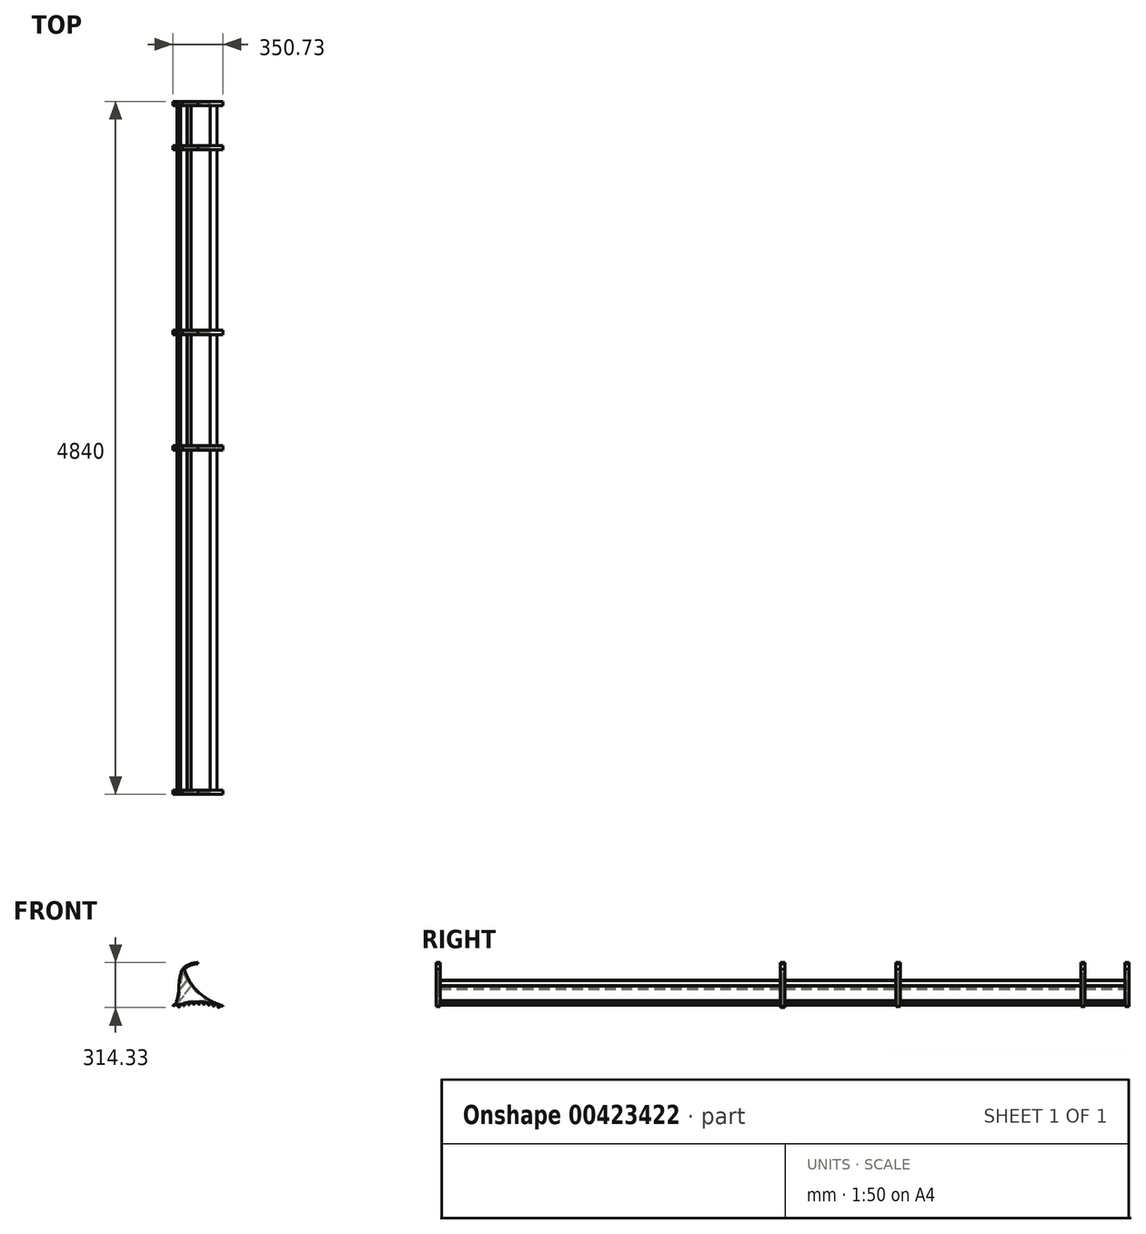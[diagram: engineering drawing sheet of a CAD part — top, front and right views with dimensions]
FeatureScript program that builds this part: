
annotation { "Feature Type Name" : "Feature", "Feature Type Description" : "" }
export const myFeature = defineFeature(function(context is Context, id is Id, definition is map)
    precondition{}
    {
        {
            var Q0;
            Q0=qCreatedBy(makeId("Front.planeOp"),FACE);
            var sketch = newSketch(context, id + "F0", { "sketchPlane" : qUnion([Q0])});
            skCircle(sketch, "E0", {"center": v(0, 0) * mm, "radius": 462.5 * mm, "construction": true});
            skLineSegment(sketch, "E1", {"start": v(0, 0) * mm, "end": v(0, 462.5) * mm, "construction": true});
            skPoint(sketch, "E2", {"position": v(0, 737.5) * mm});
            skPoint(sketch, "E3", {"position": v(-110, 692.5) * mm});
            skPoint(sketch, "E4", {"position": v(0, 729.5) * mm});
            skPoint(sketch, "E5", {"position": v(-97, 692.5) * mm});
            skLineSegment(sketch, "E6", {"start": v(0, 0) * mm, "end": v(-172.02, 429.32) * mm, "construction": true});
            skLineSegment(sketch, "E7", {"start": v(-172.02, 429.32) * mm, "end": v(-176.48, 440.46) * mm, "construction": true});
            skPoint(sketch, "E8", {"position": v(-174.25, 434.9) * mm});
            skArc(sketch, "E9", {"start": v(-174.25, 434.9) * mm, "mid": v(-160.23, 440.25) * mm, "end": v(-146.06, 445.15) * mm});
            skArc(sketch, "E10", {"start": v(-176.48, 440.46) * mm, "mid": v(-166.98, 444.15) * mm, "end": v(-157.4, 447.63) * mm});
            skLineSegment(sketch, "E11", {"start": v(-176.48, 440.46) * mm, "end": v(-174.25, 434.9) * mm});
            skLineSegment(sketch, "E12", {"start": v(0, 0) * mm, "end": v(-146.06, 445.15) * mm, "construction": true});
            skLineSegment(sketch, "E13", {"start": v(-146.06, 445.15) * mm, "end": v(-148.66, 453.08) * mm, "construction": true});
            skPoint(sketch, "E14.MirrorP", {"position": v(174.25, 434.9) * mm});
            skLineSegment(sketch, "E15.MirrorCS", {"start": v(146.06, 445.15) * mm, "end": v(148.66, 453.08) * mm, "construction": true});
            skLineSegment(sketch, "E16.MirrorCS", {"start": v(172.02, 429.32) * mm, "end": v(176.48, 440.46) * mm, "construction": true});
            skLineSegment(sketch, "E17.MirrorCS", {"start": v(0, 0) * mm, "end": v(172.02, 429.32) * mm, "construction": true});
            skLineSegment(sketch, "E18.MirrorCS", {"start": v(0, 0) * mm, "end": v(146.06, 445.15) * mm, "construction": true});
            skArc(sketch, "E19", {"start": v(146.06, 445.15) * mm, "mid": v(160.23, 440.25) * mm, "end": v(174.25, 434.9) * mm});
            skLineSegment(sketch, "E20", {"start": v(174.25, 434.9) * mm, "end": v(172.02, 429.32) * mm});
            skPoint(sketch, "E21", {"position": v(131.78, 443.33) * mm});
            skPoint(sketch, "E22", {"position": v(144.19, 439.45) * mm});
            skArc(sketch, "E23", {"start": v(131.78, 443.33) * mm, "mid": v(152.06, 436.79) * mm, "end": v(172.02, 429.32) * mm});
            skLineSegment(sketch, "E24", {"start": v(-157.4, 692.5) * mm, "end": v(-110, 692.5) * mm, "construction": true});
            skPoint(sketch, "E25", {"position": v(-133.7, 692.5) * mm});
            skLineSegment(sketch, "E26", {"start": v(-157.4, 692.5) * mm, "end": v(-157.4, 447.63) * mm, "construction": true});
            skPoint(sketch, "E27", {"position": v(-157.4, 570.07) * mm});
            skPoint(sketch, "E28", {"position": v(-133.7, 570.07) * mm});
            skArc(sketch, "E29", {"start": v(-157.4, 447.63) * mm, "mid": v(-139.68, 507.71) * mm, "end": v(-133.7, 570.07) * mm});
            skArc(sketch, "E30", {"start": v(-110, 692.5) * mm, "mid": v(-127.72, 632.42) * mm, "end": v(-133.7, 570.07) * mm});
            skArc(sketch, "E31", {"start": v(0, 737.5) * mm, "mid": v(-59.42, 725.82) * mm, "end": v(-110, 692.5) * mm});
            skLineSegment(sketch, "E32", {"start": v(0, 737.5) * mm, "end": v(0, 729.5) * mm});
            skArc(sketch, "E33", {"start": v(0, 729.5) * mm, "mid": v(-51.9, 719.94) * mm, "end": v(-97, 692.5) * mm});
            skArc(sketch, "E34", {"start": v(-97, 692.5) * mm, "mid": v(-5.55, 539.27) * mm, "end": v(146.06, 445.15) * mm});
            skArc(sketch, "E35", {"start": v(-146.06, 445.15) * mm, "mid": v(-127.1, 506.34) * mm, "end": v(-120.7, 570.07) * mm});
            skArc(sketch, "E36", {"start": v(-103.63, 668.34) * mm, "mid": v(-116.4, 619.94) * mm, "end": v(-120.7, 570.07) * mm});
            skPoint(sketch, "E37", {"position": v(-118.63, 668.34) * mm});
            skPoint(sketch, "E38", {"position": v(-88.63, 668.34) * mm});
            skLineSegment(sketch, "E39", {"start": v(-118.63, 668.34) * mm, "end": v(-88.63, 668.34) * mm, "construction": true});
            skArc(sketch, "E40", {"start": v(-103.63, 668.34) * mm, "mid": v(-10.1, 530.54) * mm, "end": v(131.78, 443.33) * mm});
            skLineSegment(sketch, "E41", {"start": v(-146.06, 445.15) * mm, "end": v(-47.75, 572) * mm});
            skLineSegment(sketch, "E42", {"start": v(-50.29, 575.26) * mm, "end": v(-140.74, 458.55) * mm});
            skLineSegment(sketch, "E43", {"start": v(-121.26, 551.05) * mm, "end": v(-74.81, 611) * mm});
            skLineSegment(sketch, "E44", {"start": v(-120.92, 558.02) * mm, "end": v(-77.02, 614.67) * mm});
            skPoint(sketch, "E45.1.14", {"position": v(-146.06, 445.15) * mm});
            skPoint(sketch, "E45.1.28", {"position": v(-144.2, 439.45) * mm});
            skArc(sketch, "E45.1.30", {"start": v(-184.02, 424.31) * mm, "mid": v(-164.28, 432.34) * mm, "end": v(-144.2, 439.45) * mm});
            skArc(sketch, "E45.1.32", {"start": v(-174.25, 434.89) * mm, "mid": v(-160.24, 440.24) * mm, "end": v(-146.06, 445.15) * mm});
            skLineSegment(sketch, "E45.1.37", {"start": v(-174.25, 434.89) * mm, "end": v(-177.36, 442.64) * mm, "construction": true});
            skLineSegment(sketch, "E45.1.39", {"start": v(-146.06, 445.15) * mm, "end": v(-144.2, 439.45) * mm});
            skLineSegment(sketch, "E45.1.40", {"start": v(-148.25, 446.82) * mm, "end": v(-152, 458.23) * mm, "construction": true});
            skPoint(sketch, "E45.8.8", {"position": v(146.06, 445.15) * mm});
            skPoint(sketch, "E45.8.26", {"position": v(144.2, 439.45) * mm});
            skLineSegment(sketch, "E45.8.33", {"start": v(144.2, 439.45) * mm, "end": v(147.93, 450.85) * mm, "construction": true});
            skArc(sketch, "E45.8.35", {"start": v(146.06, 445.15) * mm, "mid": v(160.24, 440.24) * mm, "end": v(174.25, 434.89) * mm});
            skLineSegment(sketch, "E45.8.36", {"start": v(147.93, 450.85) * mm, "end": v(146.06, 445.15) * mm});
            skLineSegment(sketch, "E45.8.38", {"start": v(174.25, 434.89) * mm, "end": v(177.36, 442.64) * mm, "construction": true});
            skArc(sketch, "E46", {"start": v(-144.2, 439.45) * mm, "mid": v(-6.5, 462.45) * mm, "end": v(131.78, 443.33) * mm});
            skPoint(sketch, "E47", {"position": v(-135.64, 442.16) * mm});
            skPoint(sketch, "E48", {"position": v(-127.05, 444.7) * mm});
            skLineSegment(sketch, "E49", {"start": v(-135.64, 442.16) * mm, "end": v(0, 0) * mm, "construction": true});
            skPoint(sketch, "E50", {"position": v(-133.45, 435) * mm});
            skArc(sketch, "E51", {"start": v(-133.45, 435) * mm, "mid": v(-129.9, 436.05) * mm, "end": v(-126.36, 437.09) * mm, "construction": true});
            skArc(sketch, "E52", {"start": v(-133.45, 435) * mm, "mid": v(-137.26, 433.8) * mm, "end": v(-141.07, 432.58) * mm, "construction": true});
            skPoint(sketch, "E53", {"position": v(-129.9, 436.05) * mm});
            skPoint(sketch, "E54", {"position": v(-137.26, 433.8) * mm});
            skLineSegment(sketch, "E55", {"start": v(0, 0) * mm, "end": v(-127.05, 444.7) * mm, "construction": true});
            skLineSegment(sketch, "E56", {"start": v(-127.05, 444.7) * mm, "end": v(-129.19, 452.2) * mm, "construction": true});
            skArc(sketch, "E57", {"start": v(-144.2, 439.45) * mm, "mid": v(-141, 436.28) * mm, "end": v(-137.26, 433.8) * mm});
            skArc(sketch, "E58", {"start": v(-129.9, 436.05) * mm, "mid": v(-127.14, 439.94) * mm, "end": v(-127.05, 444.7) * mm});
            skArc(sketch, "E59", {"start": v(-137.26, 433.8) * mm, "mid": v(-132.9, 432.7) * mm, "end": v(-129.9, 436.05) * mm});
            skLineSegment(sketch, "E60.anchor1", {"start": v(-2.2, 7.17) * mm, "end": v(-137.26, 433.8) * mm, "construction": true});
            skLineSegment(sketch, "E60.anchor2", {"start": v(-2.2, 7.17) * mm, "end": v(152.56, 427.06) * mm, "construction": true});
            skArc(sketch, "E61", {"start": v(-143.34, 448.66) * mm, "mid": v(-30, 470.04) * mm, "end": v(85.14, 463.24) * mm});
            skLineSegment(sketch, "E62", {"start": v(-129.19, 452.2) * mm, "end": v(-135.25, 459.1) * mm});
            skLineSegment(sketch, "E63", {"start": v(-44.52, 468.9) * mm, "end": v(-28.74, 549.6) * mm});
            skLineSegment(sketch, "E64", {"start": v(-30, 470.04) * mm, "end": v(-17.8, 538.11) * mm});
            skPoint(sketch, "E65", {"position": v(163.66, 432.58) * mm});
            skPoint(sketch, "E66", {"position": v(155.24, 435.67) * mm});
            skLineSegment(sketch, "E67", {"start": v(155.24, 435.67) * mm, "end": v(154.15, 432.04) * mm, "construction": true});
            skArc(sketch, "E68.1.0", {"start": v(-110.27, 449.15) * mm, "mid": v(-107.34, 445.75) * mm, "end": v(-103.8, 442.98) * mm});
            skArc(sketch, "E68.1.1", {"start": v(-103.8, 442.98) * mm, "mid": v(-99.54, 441.55) * mm, "end": v(-96.29, 444.66) * mm});
            skArc(sketch, "E68.1.2", {"start": v(-96.29, 444.66) * mm, "mid": v(-93.23, 448.32) * mm, "end": v(-92.77, 453.07) * mm});
            skPoint(sketch, "E68.1.3", {"position": v(-92.77, 453.07) * mm});
            skPoint(sketch, "E68.1.4", {"position": v(-110.27, 449.15) * mm});
            skArc(sketch, "E68.2.0", {"start": v(-75.7, 456.2) * mm, "mid": v(-73.04, 452.58) * mm, "end": v(-69.72, 449.55) * mm});
            skArc(sketch, "E68.2.1", {"start": v(-69.72, 449.55) * mm, "mid": v(-65.58, 447.8) * mm, "end": v(-62.1, 450.64) * mm});
            skArc(sketch, "E68.2.2", {"start": v(-62.1, 450.64) * mm, "mid": v(-58.77, 454.05) * mm, "end": v(-57.94, 458.74) * mm});
            skPoint(sketch, "E68.2.3", {"position": v(-57.94, 458.74) * mm});
            skPoint(sketch, "E68.2.4", {"position": v(-75.7, 456.2) * mm});
            skPoint(sketch, "E68.center", {"position": v(-2.2, 7.17) * mm});
            skLineSegment(sketch, "E68.anchor2", {"start": v(-2.2, 7.17) * mm, "end": v(136, 432.8) * mm, "construction": true});
            skArc(sketch, "E69.3.3.0", {"start": v(-40.68, 460.54) * mm, "mid": v(-38.3, 456.73) * mm, "end": v(-35.24, 453.45) * mm});
            skArc(sketch, "E69.4.3.0", {"start": v(-35.24, 453.45) * mm, "mid": v(-31.25, 451.38) * mm, "end": v(-27.56, 453.94) * mm});
            skArc(sketch, "E69.8.3.0", {"start": v(-27.56, 453.94) * mm, "mid": v(-23.97, 457.09) * mm, "end": v(-22.78, 461.7) * mm});
            skPoint(sketch, "E69.12.3.0", {"position": v(-22.78, 461.7) * mm});
            skPoint(sketch, "E69.13.3.0", {"position": v(-40.68, 460.54) * mm});
            skArc(sketch, "E69.3.4.0", {"start": v(-5.43, 462.16) * mm, "mid": v(-3.36, 458.17) * mm, "end": v(-0.56, 454.67) * mm});
            skArc(sketch, "E69.4.4.0", {"start": v(-0.56, 454.67) * mm, "mid": v(3.26, 452.3) * mm, "end": v(7.14, 454.57) * mm});
            skArc(sketch, "E69.8.4.0", {"start": v(7.14, 454.57) * mm, "mid": v(10.96, 457.42) * mm, "end": v(12.5, 461.93) * mm});
            skPoint(sketch, "E69.12.4.0", {"position": v(12.5, 461.93) * mm});
            skPoint(sketch, "E69.13.4.0", {"position": v(-5.43, 462.16) * mm});
            skArc(sketch, "E69.3.5.0", {"start": v(29.84, 461.04) * mm, "mid": v(31.59, 456.9) * mm, "end": v(34.12, 453.2) * mm});
            skArc(sketch, "E69.4.5.0", {"start": v(34.12, 453.2) * mm, "mid": v(37.74, 450.53) * mm, "end": v(41.78, 452.5) * mm});
            skArc(sketch, "E69.8.5.0", {"start": v(41.78, 452.5) * mm, "mid": v(45.8, 455.05) * mm, "end": v(47.7, 459.43) * mm});
            skPoint(sketch, "E69.12.5.0", {"position": v(47.7, 459.43) * mm});
            skPoint(sketch, "E69.13.5.0", {"position": v(29.84, 461.04) * mm});
            skArc(sketch, "E69.3.6.0", {"start": v(64.91, 457.2) * mm, "mid": v(66.34, 452.94) * mm, "end": v(68.57, 449.04) * mm});
            skArc(sketch, "E69.4.6.0", {"start": v(68.57, 449.04) * mm, "mid": v(71.97, 446.1) * mm, "end": v(76.16, 447.75) * mm});
            skArc(sketch, "E69.8.6.0", {"start": v(76.16, 447.75) * mm, "mid": v(80.37, 449.98) * mm, "end": v(82.6, 454.2) * mm});
            skPoint(sketch, "E69.12.6.0", {"position": v(82.6, 454.2) * mm});
            skPoint(sketch, "E69.13.6.0", {"position": v(64.91, 457.2) * mm});
            skArc(sketch, "E69.3.7.0", {"start": v(99.59, 450.64) * mm, "mid": v(100.68, 446.28) * mm, "end": v(102.6, 442.23) * mm});
            skArc(sketch, "E69.4.7.0", {"start": v(102.6, 442.23) * mm, "mid": v(105.76, 439.04) * mm, "end": v(110.06, 440.35) * mm});
            skArc(sketch, "E69.8.7.0", {"start": v(110.06, 440.35) * mm, "mid": v(114.43, 442.25) * mm, "end": v(116.98, 446.29) * mm});
            skPoint(sketch, "E69.12.7.0", {"position": v(116.98, 446.29) * mm});
            skPoint(sketch, "E69.13.7.0", {"position": v(99.59, 450.64) * mm});
            skArc(sketch, "E69.3.8.0", {"start": v(133.64, 441.42) * mm, "mid": v(134.4, 437) * mm, "end": v(136, 432.8) * mm});
            skArc(sketch, "E69.4.8.0", {"start": v(136, 432.8) * mm, "mid": v(138.9, 429.37) * mm, "end": v(143.3, 430.35) * mm});
            skArc(sketch, "E69.8.8.0", {"start": v(143.3, 430.35) * mm, "mid": v(147.8, 431.9) * mm, "end": v(150.65, 435.73) * mm});
            skPoint(sketch, "E69.12.8.0", {"position": v(150.65, 435.73) * mm});
            skPoint(sketch, "E69.13.8.0", {"position": v(133.64, 441.42) * mm});
            skSolve(sketch);
        }
        {
            var Q0;
            {var subQ14=sQuery(id+"F0.wireOp",EDGE,"E9");Q0=makeQuery(id+"F0.imprint","IMPRINT",FACE,{"disambiguationData":[TD([[makeQuery(id+"F0.imprint","IMPRINT",EDGE,{"derivedFrom":subQ14}),1.0]])]});}
            var Q1;
            {var subQ0=sQuery(id+"F0.wireOp",EDGE,"E43");Q1=makeQuery(id+"F0.imprint","IMPRINT",FACE,{"disambiguationData":[TD([[makeQuery(id+"F0.imprint","IMPRINT",EDGE,{"derivedFrom":subQ0}),1.0]])]});}
            var Q2;
            {var subQ0=sQuery(id+"F0.wireOp",EDGE,"E41");Q2=makeQuery(id+"F0.imprint","IMPRINT",FACE,{"disambiguationData":[TD([[makeQuery(id+"F0.imprint","IMPRINT",EDGE,{"derivedFrom":subQ0}),1.0]])]});}
            extrude(context, id + "F1", {"entities" : qUnion([Q0, Q1, Q2]), "depth" : 4840 * mm});
        }
        {
            var Q0;
            Q0=qCreatedBy(makeId("Front.planeOp"),FACE);
            cPlane(context, id + "F2", {"entities" : qUnion([Q0]), "cplaneType" : CPlaneType.OFFSET, "offset" : 4840 * mm, "width" : 150 * mm, "height" : 150 * mm});
        }
        {
            var Q0;
            Q0=qCreatedBy(makeId("Front.planeOp"),FACE);
            cPlane(context, id + "F3", {"entities" : qUnion([Q0]), "cplaneType" : CPlaneType.OFFSET, "offset" : 1613.33 * mm, "width" : 150 * mm, "height" : 150 * mm});
        }
        {
            var Q0;
            Q0=qCreatedBy(makeId("Front.planeOp"),FACE);
            cPlane(context, id + "F4", {"entities" : qUnion([Q0]), "cplaneType" : CPlaneType.OFFSET, "offset" : ((484 / 3) + (484 / 3)) * mm, "width" : 150 * mm, "height" : 150 * mm});
        }
        {
            var Q0;
            Q0=qCreatedBy(makeId("Front.planeOp"),FACE);
            var sketch = newSketch(context, id + "F5", { "sketchPlane" : qUnion([Q0])});
            skCircle(sketch, "E70", {"center": v(0, 0) * mm, "radius": 462.5 * mm, "construction": true});
            skLineSegment(sketch, "E71", {"start": v(0, 0) * mm, "end": v(0, 462.5) * mm, "construction": true});
            skPoint(sketch, "E72", {"position": v(0, 737.5) * mm});
            skPoint(sketch, "E73", {"position": v(-110, 692.5) * mm});
            skPoint(sketch, "E74", {"position": v(0, 729.5) * mm});
            skPoint(sketch, "E75", {"position": v(-97, 692.5) * mm});
            skLineSegment(sketch, "E76", {"start": v(0, 0) * mm, "end": v(-172.02, 429.32) * mm, "construction": true});
            skLineSegment(sketch, "E77", {"start": v(-172.02, 429.32) * mm, "end": v(-176.48, 440.46) * mm, "construction": true});
            skPoint(sketch, "E78", {"position": v(-174.25, 434.9) * mm});
            skArc(sketch, "E79", {"start": v(-174.25, 434.9) * mm, "mid": v(-160.23, 440.25) * mm, "end": v(-146.06, 445.15) * mm});
            skArc(sketch, "E80", {"start": v(-176.48, 440.46) * mm, "mid": v(-166.98, 444.15) * mm, "end": v(-157.4, 447.63) * mm});
            skLineSegment(sketch, "E81", {"start": v(-176.48, 440.46) * mm, "end": v(-174.25, 434.9) * mm});
            skLineSegment(sketch, "E82", {"start": v(0, 0) * mm, "end": v(-146.06, 445.15) * mm, "construction": true});
            skLineSegment(sketch, "E83", {"start": v(-146.06, 445.15) * mm, "end": v(-148.66, 453.08) * mm, "construction": true});
            skPoint(sketch, "E84.MirrorP", {"position": v(174.25, 434.9) * mm});
            skLineSegment(sketch, "E85.MirrorCS", {"start": v(146.06, 445.15) * mm, "end": v(148.66, 453.08) * mm, "construction": true});
            skLineSegment(sketch, "E86.MirrorCS", {"start": v(172.02, 429.32) * mm, "end": v(176.48, 440.46) * mm, "construction": true});
            skLineSegment(sketch, "E87.MirrorCS", {"start": v(0, 0) * mm, "end": v(172.02, 429.32) * mm, "construction": true});
            skLineSegment(sketch, "E88.MirrorCS", {"start": v(0, 0) * mm, "end": v(146.06, 445.15) * mm, "construction": true});
            skArc(sketch, "E89", {"start": v(146.06, 445.15) * mm, "mid": v(160.23, 440.25) * mm, "end": v(174.25, 434.9) * mm});
            skLineSegment(sketch, "E90", {"start": v(174.25, 434.9) * mm, "end": v(172.02, 429.32) * mm});
            skPoint(sketch, "E91", {"position": v(131.78, 443.33) * mm});
            skPoint(sketch, "E92", {"position": v(144.19, 439.45) * mm});
            skArc(sketch, "E93", {"start": v(131.78, 443.33) * mm, "mid": v(152.06, 436.79) * mm, "end": v(172.02, 429.32) * mm});
            skLineSegment(sketch, "E94", {"start": v(-157.4, 692.5) * mm, "end": v(-110, 692.5) * mm, "construction": true});
            skPoint(sketch, "E95", {"position": v(-133.7, 692.5) * mm});
            skLineSegment(sketch, "E96", {"start": v(-157.4, 692.5) * mm, "end": v(-157.4, 447.63) * mm, "construction": true});
            skPoint(sketch, "E97", {"position": v(-157.4, 570.07) * mm});
            skPoint(sketch, "E98", {"position": v(-133.7, 570.07) * mm});
            skArc(sketch, "E99", {"start": v(-157.4, 447.63) * mm, "mid": v(-139.68, 507.71) * mm, "end": v(-133.7, 570.07) * mm});
            skArc(sketch, "E100", {"start": v(-110, 692.5) * mm, "mid": v(-127.72, 632.42) * mm, "end": v(-133.7, 570.07) * mm});
            skArc(sketch, "E101", {"start": v(0, 737.5) * mm, "mid": v(-59.42, 725.82) * mm, "end": v(-110, 692.5) * mm});
            skLineSegment(sketch, "E102", {"start": v(0, 737.5) * mm, "end": v(0, 729.5) * mm});
            skArc(sketch, "E103", {"start": v(0, 729.5) * mm, "mid": v(-51.9, 719.94) * mm, "end": v(-97, 692.5) * mm});
            skArc(sketch, "E104", {"start": v(-97, 692.5) * mm, "mid": v(-5.55, 539.27) * mm, "end": v(146.06, 445.15) * mm});
            skArc(sketch, "E105", {"start": v(-146.06, 445.15) * mm, "mid": v(-127.1, 506.34) * mm, "end": v(-120.7, 570.07) * mm});
            skArc(sketch, "E106", {"start": v(-103.63, 668.34) * mm, "mid": v(-116.4, 619.94) * mm, "end": v(-120.7, 570.07) * mm});
            skPoint(sketch, "E107", {"position": v(-118.63, 668.34) * mm});
            skPoint(sketch, "E108", {"position": v(-88.63, 668.34) * mm});
            skLineSegment(sketch, "E109", {"start": v(-118.63, 668.34) * mm, "end": v(-88.63, 668.34) * mm, "construction": true});
            skArc(sketch, "E110", {"start": v(-103.63, 668.34) * mm, "mid": v(-10.1, 530.54) * mm, "end": v(131.78, 443.33) * mm});
            skPoint(sketch, "E111.1.14", {"position": v(-146.06, 445.15) * mm});
            skPoint(sketch, "E111.1.28", {"position": v(-144.2, 439.45) * mm});
            skArc(sketch, "E111.1.30", {"start": v(-184.02, 424.31) * mm, "mid": v(-164.28, 432.34) * mm, "end": v(-144.2, 439.45) * mm});
            skArc(sketch, "E111.1.32", {"start": v(-174.25, 434.89) * mm, "mid": v(-160.24, 440.24) * mm, "end": v(-146.06, 445.15) * mm});
            skLineSegment(sketch, "E111.1.37", {"start": v(-174.25, 434.89) * mm, "end": v(-177.36, 442.64) * mm, "construction": true});
            skLineSegment(sketch, "E111.1.39", {"start": v(-146.06, 445.15) * mm, "end": v(-144.2, 439.45) * mm});
            skLineSegment(sketch, "E111.1.40", {"start": v(-143.86, 438.33) * mm, "end": v(-147.6, 449.73) * mm, "construction": true});
            skPoint(sketch, "E111.8.8", {"position": v(146.06, 448.35) * mm});
            skPoint(sketch, "E111.8.26", {"position": v(144.2, 442.65) * mm});
            skLineSegment(sketch, "E111.8.33", {"start": v(144.2, 442.65) * mm, "end": v(147.93, 454.05) * mm, "construction": true});
            skArc(sketch, "E111.8.35", {"start": v(146.06, 448.35) * mm, "mid": v(160.24, 443.45) * mm, "end": v(174.25, 438.1) * mm});
            skLineSegment(sketch, "E111.8.36", {"start": v(147.93, 454.05) * mm, "end": v(146.06, 448.35) * mm});
            skLineSegment(sketch, "E111.8.38", {"start": v(174.25, 438.1) * mm, "end": v(177.36, 445.84) * mm, "construction": true});
            skArc(sketch, "E112", {"start": v(-144.2, 439.45) * mm, "mid": v(-6.5, 462.45) * mm, "end": v(131.78, 443.33) * mm});
            skPoint(sketch, "E113", {"position": v(-135.64, 442.16) * mm});
            skPoint(sketch, "E114", {"position": v(-127.05, 444.7) * mm});
            skLineSegment(sketch, "E115", {"start": v(-135.64, 442.16) * mm, "end": v(0, 0) * mm, "construction": true});
            skPoint(sketch, "E116", {"position": v(-131.25, 427.82) * mm});
            skArc(sketch, "E117", {"start": v(-131.25, 427.82) * mm, "mid": v(-127.7, 428.89) * mm, "end": v(-124.16, 429.93) * mm, "construction": true});
            skArc(sketch, "E118", {"start": v(-131.25, 427.82) * mm, "mid": v(-135.06, 426.63) * mm, "end": v(-138.87, 425.4) * mm, "construction": true});
            skPoint(sketch, "E119", {"position": v(-127.7, 428.89) * mm});
            skPoint(sketch, "E120", {"position": v(-135.06, 426.63) * mm});
            skLineSegment(sketch, "E121", {"start": v(0, 0) * mm, "end": v(-127.05, 444.7) * mm, "construction": true});
            skLineSegment(sketch, "E122", {"start": v(-127.05, 444.7) * mm, "end": v(-129.19, 452.2) * mm, "construction": true});
            skArc(sketch, "E123", {"start": v(-144.2, 439.45) * mm, "mid": v(-140.77, 432.23) * mm, "end": v(-135.06, 426.63) * mm});
            skArc(sketch, "E124", {"start": v(-127.7, 428.89) * mm, "mid": v(-126.1, 436.75) * mm, "end": v(-127.05, 444.7) * mm});
            skArc(sketch, "E125", {"start": v(-135.06, 426.63) * mm, "mid": v(-131.17, 427.05) * mm, "end": v(-127.7, 428.89) * mm});
            skLineSegment(sketch, "E126.anchor1", {"start": v(0, 0) * mm, "end": v(-135.06, 426.63) * mm, "construction": true});
            skLineSegment(sketch, "E126.anchor2", {"start": v(0, 0) * mm, "end": v(154.76, 419.89) * mm, "construction": true});
            skArc(sketch, "E127", {"start": v(-144.79, 448.2) * mm, "mid": v(-30.76, 470) * mm, "end": v(85.14, 463.24) * mm});
            skPoint(sketch, "E128", {"position": v(163.66, 432.58) * mm});
            skPoint(sketch, "E129", {"position": v(155.24, 435.67) * mm});
            skLineSegment(sketch, "E130", {"start": v(155.24, 435.67) * mm, "end": v(154.15, 432.04) * mm, "construction": true});
            skArc(sketch, "E131.1.0", {"start": v(-109.7, 449.3) * mm, "mid": v(-106.85, 441.83) * mm, "end": v(-101.6, 435.81) * mm});
            skArc(sketch, "E131.1.1", {"start": v(-101.6, 435.81) * mm, "mid": v(-97.68, 435.93) * mm, "end": v(-94.1, 437.5) * mm});
            skArc(sketch, "E131.1.2", {"start": v(-94.1, 437.5) * mm, "mid": v(-91.88, 445.2) * mm, "end": v(-92.2, 453.22) * mm});
            skPoint(sketch, "E131.1.3", {"position": v(-92.2, 453.22) * mm});
            skPoint(sketch, "E131.1.4", {"position": v(-109.7, 449.3) * mm});
            skArc(sketch, "E131.2.0", {"start": v(-74.56, 456.45) * mm, "mid": v(-72.3, 448.79) * mm, "end": v(-67.52, 442.38) * mm});
            skArc(sketch, "E131.2.1", {"start": v(-67.52, 442.38) * mm, "mid": v(-63.6, 442.18) * mm, "end": v(-59.9, 443.47) * mm});
            skArc(sketch, "E131.2.2", {"start": v(-59.9, 443.47) * mm, "mid": v(-57.1, 450.99) * mm, "end": v(-56.8, 459) * mm});
            skPoint(sketch, "E131.2.3", {"position": v(-56.8, 459) * mm});
            skPoint(sketch, "E131.2.4", {"position": v(-74.56, 456.45) * mm});
            skLineSegment(sketch, "E131.anchor2", {"start": v(0, 0) * mm, "end": v(138.2, 425.63) * mm, "construction": true});
            skArc(sketch, "E132.3.3.0", {"start": v(-38.96, 460.86) * mm, "mid": v(-37.3, 453.04) * mm, "end": v(-33.04, 446.28) * mm});
            skArc(sketch, "E132.4.3.0", {"start": v(-33.04, 446.28) * mm, "mid": v(-29.15, 445.78) * mm, "end": v(-25.36, 446.78) * mm});
            skArc(sketch, "E132.8.3.0", {"start": v(-25.36, 446.78) * mm, "mid": v(-21.98, 454.05) * mm, "end": v(-21.07, 462.02) * mm});
            skPoint(sketch, "E132.12.3.0", {"position": v(-21.07, 462.02) * mm});
            skPoint(sketch, "E132.13.3.0", {"position": v(-38.96, 460.86) * mm});
            skArc(sketch, "E132.3.4.0", {"start": v(-3.13, 462.49) * mm, "mid": v(-2.08, 454.57) * mm, "end": v(1.64, 447.5) * mm});
            skArc(sketch, "E132.4.4.0", {"start": v(1.64, 447.5) * mm, "mid": v(5.48, 446.7) * mm, "end": v(9.34, 447.4) * mm});
            skArc(sketch, "E132.8.4.0", {"start": v(9.34, 447.4) * mm, "mid": v(13.27, 454.4) * mm, "end": v(14.8, 462.26) * mm});
            skPoint(sketch, "E132.12.4.0", {"position": v(14.8, 462.26) * mm});
            skPoint(sketch, "E132.13.4.0", {"position": v(-3.13, 462.49) * mm});
            skArc(sketch, "E132.3.5.0", {"start": v(32.72, 461.34) * mm, "mid": v(33.15, 453.36) * mm, "end": v(36.32, 446.02) * mm});
            skArc(sketch, "E132.4.5.0", {"start": v(36.32, 446.02) * mm, "mid": v(40.08, 444.93) * mm, "end": v(43.98, 445.33) * mm});
            skArc(sketch, "E132.8.5.0", {"start": v(43.98, 445.33) * mm, "mid": v(48.44, 452) * mm, "end": v(50.57, 459.73) * mm});
            skPoint(sketch, "E132.12.5.0", {"position": v(50.57, 459.73) * mm});
            skPoint(sketch, "E132.13.5.0", {"position": v(32.72, 461.34) * mm});
            skArc(sketch, "E132.3.6.0", {"start": v(68.37, 457.42) * mm, "mid": v(68.18, 449.43) * mm, "end": v(70.77, 441.87) * mm});
            skArc(sketch, "E132.4.6.0", {"start": v(70.77, 441.87) * mm, "mid": v(74.44, 440.49) * mm, "end": v(78.36, 440.59) * mm});
            skArc(sketch, "E132.8.6.0", {"start": v(78.36, 440.59) * mm, "mid": v(83.32, 446.88) * mm, "end": v(86.05, 454.42) * mm});
            skPoint(sketch, "E132.12.6.0", {"position": v(86.05, 454.42) * mm});
            skPoint(sketch, "E132.13.6.0", {"position": v(68.37, 457.42) * mm});
            skArc(sketch, "E132.3.7.0", {"start": v(103.6, 450.75) * mm, "mid": v(102.8, 442.8) * mm, "end": v(104.8, 435.06) * mm});
            skArc(sketch, "E132.4.7.0", {"start": v(104.8, 435.06) * mm, "mid": v(108.35, 433.4) * mm, "end": v(112.26, 433.19) * mm});
            skArc(sketch, "E132.8.7.0", {"start": v(112.26, 433.19) * mm, "mid": v(117.7, 439.08) * mm, "end": v(121, 446.4) * mm});
            skPoint(sketch, "E132.12.7.0", {"position": v(121, 446.4) * mm});
            skPoint(sketch, "E132.13.7.0", {"position": v(103.6, 450.75) * mm});
            skArc(sketch, "E132.3.8.0", {"start": v(138.22, 441.36) * mm, "mid": v(136.8, 433.5) * mm, "end": v(138.2, 425.63) * mm});
            skArc(sketch, "E132.4.8.0", {"start": v(138.2, 425.63) * mm, "mid": v(141.6, 423.7) * mm, "end": v(145.5, 423.19) * mm});
            skArc(sketch, "E132.8.8.0", {"start": v(145.5, 423.19) * mm, "mid": v(151.37, 428.64) * mm, "end": v(155.23, 435.67) * mm});
            skPoint(sketch, "E132.12.8.0", {"position": v(155.23, 435.67) * mm});
            skPoint(sketch, "E132.13.8.0", {"position": v(138.22, 441.36) * mm});
            skSolve(sketch);
        }
        {
            var Q0;
            Q0=qCreatedBy(id+"F3.planeOp",FACE);
            var sketch = newSketch(context, id + "F6", { "sketchPlane" : qUnion([Q0])});
            skCircle(sketch, "E133", {"center": v(0, 0) * mm, "radius": 462.5 * mm, "construction": true});
            skLineSegment(sketch, "E134", {"start": v(0, 0) * mm, "end": v(0, 462.5) * mm, "construction": true});
            skPoint(sketch, "E135", {"position": v(0, 737.5) * mm});
            skPoint(sketch, "E136", {"position": v(-110, 692.5) * mm});
            skPoint(sketch, "E137", {"position": v(0, 729.5) * mm});
            skPoint(sketch, "E138", {"position": v(-97, 692.5) * mm});
            skLineSegment(sketch, "E139", {"start": v(0, 0) * mm, "end": v(-172.02, 429.32) * mm, "construction": true});
            skLineSegment(sketch, "E140", {"start": v(-172.02, 429.32) * mm, "end": v(-176.48, 440.46) * mm, "construction": true});
            skPoint(sketch, "E141", {"position": v(-174.25, 434.9) * mm});
            skArc(sketch, "E142", {"start": v(-174.25, 434.9) * mm, "mid": v(-160.23, 440.25) * mm, "end": v(-146.06, 445.15) * mm});
            skArc(sketch, "E143", {"start": v(-176.48, 440.46) * mm, "mid": v(-166.98, 444.15) * mm, "end": v(-157.4, 447.63) * mm});
            skLineSegment(sketch, "E144", {"start": v(-176.48, 440.46) * mm, "end": v(-174.25, 434.9) * mm});
            skLineSegment(sketch, "E145", {"start": v(0, 0) * mm, "end": v(-146.06, 445.15) * mm, "construction": true});
            skLineSegment(sketch, "E146", {"start": v(-146.06, 445.15) * mm, "end": v(-148.66, 453.08) * mm, "construction": true});
            skPoint(sketch, "E147.MirrorP", {"position": v(174.25, 434.9) * mm});
            skLineSegment(sketch, "E148.MirrorCS", {"start": v(146.06, 445.15) * mm, "end": v(148.66, 453.08) * mm, "construction": true});
            skLineSegment(sketch, "E149.MirrorCS", {"start": v(172.02, 429.32) * mm, "end": v(176.48, 440.46) * mm, "construction": true});
            skLineSegment(sketch, "E150.MirrorCS", {"start": v(0, 0) * mm, "end": v(172.02, 429.32) * mm, "construction": true});
            skLineSegment(sketch, "E151.MirrorCS", {"start": v(0, 0) * mm, "end": v(146.06, 445.15) * mm, "construction": true});
            skArc(sketch, "E152", {"start": v(146.06, 445.15) * mm, "mid": v(160.23, 440.25) * mm, "end": v(174.25, 434.9) * mm});
            skLineSegment(sketch, "E153", {"start": v(174.25, 434.9) * mm, "end": v(172.02, 429.32) * mm});
            skPoint(sketch, "E154", {"position": v(131.78, 443.33) * mm});
            skPoint(sketch, "E155", {"position": v(144.19, 439.45) * mm});
            skArc(sketch, "E156", {"start": v(131.78, 443.33) * mm, "mid": v(152.06, 436.79) * mm, "end": v(172.02, 429.32) * mm});
            skLineSegment(sketch, "E157", {"start": v(-157.4, 692.5) * mm, "end": v(-110, 692.5) * mm, "construction": true});
            skPoint(sketch, "E158", {"position": v(-133.7, 692.5) * mm});
            skLineSegment(sketch, "E159", {"start": v(-157.4, 692.5) * mm, "end": v(-157.4, 447.63) * mm, "construction": true});
            skPoint(sketch, "E160", {"position": v(-157.4, 570.07) * mm});
            skPoint(sketch, "E161", {"position": v(-133.7, 570.07) * mm});
            skArc(sketch, "E162", {"start": v(-157.4, 447.63) * mm, "mid": v(-139.68, 507.71) * mm, "end": v(-133.7, 570.07) * mm});
            skArc(sketch, "E163", {"start": v(-110, 692.5) * mm, "mid": v(-127.72, 632.42) * mm, "end": v(-133.7, 570.07) * mm});
            skArc(sketch, "E164", {"start": v(0, 737.5) * mm, "mid": v(-59.42, 725.82) * mm, "end": v(-110, 692.5) * mm});
            skLineSegment(sketch, "E165", {"start": v(0, 737.5) * mm, "end": v(0, 729.5) * mm});
            skArc(sketch, "E166", {"start": v(0, 729.5) * mm, "mid": v(-51.9, 719.94) * mm, "end": v(-97, 692.5) * mm});
            skArc(sketch, "E167", {"start": v(-97, 692.5) * mm, "mid": v(-5.55, 539.27) * mm, "end": v(146.06, 445.15) * mm});
            skArc(sketch, "E168", {"start": v(-146.06, 445.15) * mm, "mid": v(-127.1, 506.34) * mm, "end": v(-120.7, 570.07) * mm});
            skArc(sketch, "E169", {"start": v(-103.63, 668.34) * mm, "mid": v(-116.4, 619.94) * mm, "end": v(-120.7, 570.07) * mm});
            skPoint(sketch, "E170", {"position": v(-118.63, 668.34) * mm});
            skPoint(sketch, "E171", {"position": v(-88.63, 668.34) * mm});
            skLineSegment(sketch, "E172", {"start": v(-118.63, 668.34) * mm, "end": v(-88.63, 668.34) * mm, "construction": true});
            skArc(sketch, "E173", {"start": v(-103.63, 668.34) * mm, "mid": v(-10.1, 530.54) * mm, "end": v(131.78, 443.33) * mm});
            skPoint(sketch, "E174.1.14", {"position": v(-146.06, 445.15) * mm});
            skPoint(sketch, "E174.1.28", {"position": v(-144.2, 439.45) * mm});
            skArc(sketch, "E174.1.30", {"start": v(-184.02, 424.31) * mm, "mid": v(-164.28, 432.34) * mm, "end": v(-144.2, 439.45) * mm});
            skArc(sketch, "E174.1.32", {"start": v(-174.25, 434.89) * mm, "mid": v(-160.24, 440.24) * mm, "end": v(-146.06, 445.15) * mm});
            skLineSegment(sketch, "E174.1.37", {"start": v(-174.25, 434.89) * mm, "end": v(-177.36, 442.64) * mm, "construction": true});
            skLineSegment(sketch, "E174.1.39", {"start": v(-146.06, 445.15) * mm, "end": v(-144.2, 439.45) * mm});
            skLineSegment(sketch, "E174.1.40", {"start": v(-143.86, 438.33) * mm, "end": v(-147.6, 449.73) * mm, "construction": true});
            skPoint(sketch, "E174.8.8", {"position": v(146.06, 448.35) * mm});
            skPoint(sketch, "E174.8.26", {"position": v(144.2, 442.65) * mm});
            skLineSegment(sketch, "E174.8.33", {"start": v(144.2, 442.65) * mm, "end": v(147.93, 454.05) * mm, "construction": true});
            skArc(sketch, "E174.8.35", {"start": v(146.06, 448.35) * mm, "mid": v(160.24, 443.45) * mm, "end": v(174.25, 438.1) * mm});
            skLineSegment(sketch, "E174.8.36", {"start": v(147.93, 454.05) * mm, "end": v(146.06, 448.35) * mm});
            skLineSegment(sketch, "E174.8.38", {"start": v(174.25, 438.1) * mm, "end": v(177.36, 445.84) * mm, "construction": true});
            skArc(sketch, "E175", {"start": v(-144.2, 439.45) * mm, "mid": v(-6.5, 462.45) * mm, "end": v(131.78, 443.33) * mm});
            skPoint(sketch, "E176", {"position": v(-135.64, 442.16) * mm});
            skPoint(sketch, "E177", {"position": v(-127.05, 444.7) * mm});
            skLineSegment(sketch, "E178", {"start": v(-135.64, 442.16) * mm, "end": v(0, 0) * mm, "construction": true});
            skPoint(sketch, "E179", {"position": v(-131.25, 427.82) * mm});
            skArc(sketch, "E180", {"start": v(-131.25, 427.82) * mm, "mid": v(-127.7, 428.89) * mm, "end": v(-124.16, 429.93) * mm, "construction": true});
            skArc(sketch, "E181", {"start": v(-131.25, 427.82) * mm, "mid": v(-135.06, 426.63) * mm, "end": v(-138.87, 425.4) * mm, "construction": true});
            skPoint(sketch, "E182", {"position": v(-127.7, 428.89) * mm});
            skPoint(sketch, "E183", {"position": v(-135.06, 426.63) * mm});
            skLineSegment(sketch, "E184", {"start": v(0, 0) * mm, "end": v(-127.05, 444.7) * mm, "construction": true});
            skLineSegment(sketch, "E185", {"start": v(-127.05, 444.7) * mm, "end": v(-129.19, 452.2) * mm, "construction": true});
            skArc(sketch, "E186", {"start": v(-144.2, 439.45) * mm, "mid": v(-140.77, 432.23) * mm, "end": v(-135.06, 426.63) * mm});
            skArc(sketch, "E187", {"start": v(-127.7, 428.89) * mm, "mid": v(-126.1, 436.75) * mm, "end": v(-127.05, 444.7) * mm});
            skArc(sketch, "E188", {"start": v(-135.06, 426.63) * mm, "mid": v(-131.17, 427.05) * mm, "end": v(-127.7, 428.89) * mm});
            skLineSegment(sketch, "E189.anchor1", {"start": v(0, 0) * mm, "end": v(-135.06, 426.63) * mm, "construction": true});
            skLineSegment(sketch, "E189.anchor2", {"start": v(0, 0) * mm, "end": v(154.76, 419.89) * mm, "construction": true});
            skArc(sketch, "E190", {"start": v(-144.79, 448.2) * mm, "mid": v(-30.76, 470) * mm, "end": v(85.14, 463.24) * mm});
            skPoint(sketch, "E191", {"position": v(163.66, 432.58) * mm});
            skPoint(sketch, "E192", {"position": v(155.24, 435.67) * mm});
            skLineSegment(sketch, "E193", {"start": v(155.24, 435.67) * mm, "end": v(154.15, 432.04) * mm, "construction": true});
            skArc(sketch, "E194.1.0", {"start": v(-109.7, 449.3) * mm, "mid": v(-106.85, 441.83) * mm, "end": v(-101.6, 435.81) * mm});
            skArc(sketch, "E194.1.1", {"start": v(-101.6, 435.81) * mm, "mid": v(-97.68, 435.93) * mm, "end": v(-94.1, 437.5) * mm});
            skArc(sketch, "E194.1.2", {"start": v(-94.1, 437.5) * mm, "mid": v(-91.88, 445.2) * mm, "end": v(-92.2, 453.22) * mm});
            skPoint(sketch, "E194.1.3", {"position": v(-92.2, 453.22) * mm});
            skPoint(sketch, "E194.1.4", {"position": v(-109.7, 449.3) * mm});
            skArc(sketch, "E194.2.0", {"start": v(-74.56, 456.45) * mm, "mid": v(-72.3, 448.79) * mm, "end": v(-67.52, 442.38) * mm});
            skArc(sketch, "E194.2.1", {"start": v(-67.52, 442.38) * mm, "mid": v(-63.6, 442.18) * mm, "end": v(-59.9, 443.47) * mm});
            skArc(sketch, "E194.2.2", {"start": v(-59.9, 443.47) * mm, "mid": v(-57.1, 450.99) * mm, "end": v(-56.8, 459) * mm});
            skPoint(sketch, "E194.2.3", {"position": v(-56.8, 459) * mm});
            skPoint(sketch, "E194.2.4", {"position": v(-74.56, 456.45) * mm});
            skLineSegment(sketch, "E194.anchor2", {"start": v(0, 0) * mm, "end": v(138.2, 425.63) * mm, "construction": true});
            skArc(sketch, "E195.3.3.0", {"start": v(-38.96, 460.86) * mm, "mid": v(-37.3, 453.04) * mm, "end": v(-33.04, 446.28) * mm});
            skArc(sketch, "E195.4.3.0", {"start": v(-33.04, 446.28) * mm, "mid": v(-29.15, 445.78) * mm, "end": v(-25.36, 446.78) * mm});
            skArc(sketch, "E195.8.3.0", {"start": v(-25.36, 446.78) * mm, "mid": v(-21.98, 454.05) * mm, "end": v(-21.07, 462.02) * mm});
            skPoint(sketch, "E195.12.3.0", {"position": v(-21.07, 462.02) * mm});
            skPoint(sketch, "E195.13.3.0", {"position": v(-38.96, 460.86) * mm});
            skArc(sketch, "E195.3.4.0", {"start": v(-3.13, 462.49) * mm, "mid": v(-2.08, 454.57) * mm, "end": v(1.64, 447.5) * mm});
            skArc(sketch, "E195.4.4.0", {"start": v(1.64, 447.5) * mm, "mid": v(5.48, 446.7) * mm, "end": v(9.34, 447.4) * mm});
            skArc(sketch, "E195.8.4.0", {"start": v(9.34, 447.4) * mm, "mid": v(13.27, 454.4) * mm, "end": v(14.8, 462.26) * mm});
            skPoint(sketch, "E195.12.4.0", {"position": v(14.8, 462.26) * mm});
            skPoint(sketch, "E195.13.4.0", {"position": v(-3.13, 462.49) * mm});
            skArc(sketch, "E195.3.5.0", {"start": v(32.72, 461.34) * mm, "mid": v(33.15, 453.36) * mm, "end": v(36.32, 446.02) * mm});
            skArc(sketch, "E195.4.5.0", {"start": v(36.32, 446.02) * mm, "mid": v(40.08, 444.93) * mm, "end": v(43.98, 445.33) * mm});
            skArc(sketch, "E195.8.5.0", {"start": v(43.98, 445.33) * mm, "mid": v(48.44, 452) * mm, "end": v(50.57, 459.73) * mm});
            skPoint(sketch, "E195.12.5.0", {"position": v(50.57, 459.73) * mm});
            skPoint(sketch, "E195.13.5.0", {"position": v(32.72, 461.34) * mm});
            skArc(sketch, "E195.3.6.0", {"start": v(68.37, 457.42) * mm, "mid": v(68.18, 449.43) * mm, "end": v(70.77, 441.87) * mm});
            skArc(sketch, "E195.4.6.0", {"start": v(70.77, 441.87) * mm, "mid": v(74.44, 440.49) * mm, "end": v(78.36, 440.59) * mm});
            skArc(sketch, "E195.8.6.0", {"start": v(78.36, 440.59) * mm, "mid": v(83.32, 446.88) * mm, "end": v(86.05, 454.42) * mm});
            skPoint(sketch, "E195.12.6.0", {"position": v(86.05, 454.42) * mm});
            skPoint(sketch, "E195.13.6.0", {"position": v(68.37, 457.42) * mm});
            skArc(sketch, "E195.3.7.0", {"start": v(103.6, 450.75) * mm, "mid": v(102.8, 442.8) * mm, "end": v(104.8, 435.06) * mm});
            skArc(sketch, "E195.4.7.0", {"start": v(104.8, 435.06) * mm, "mid": v(108.35, 433.4) * mm, "end": v(112.26, 433.19) * mm});
            skArc(sketch, "E195.8.7.0", {"start": v(112.26, 433.19) * mm, "mid": v(117.7, 439.08) * mm, "end": v(121, 446.4) * mm});
            skPoint(sketch, "E195.12.7.0", {"position": v(121, 446.4) * mm});
            skPoint(sketch, "E195.13.7.0", {"position": v(103.6, 450.75) * mm});
            skArc(sketch, "E195.3.8.0", {"start": v(138.22, 441.36) * mm, "mid": v(136.8, 433.5) * mm, "end": v(138.2, 425.63) * mm});
            skArc(sketch, "E195.4.8.0", {"start": v(138.2, 425.63) * mm, "mid": v(141.6, 423.7) * mm, "end": v(145.5, 423.19) * mm});
            skArc(sketch, "E195.8.8.0", {"start": v(145.5, 423.19) * mm, "mid": v(151.37, 428.64) * mm, "end": v(155.23, 435.67) * mm});
            skPoint(sketch, "E195.12.8.0", {"position": v(155.23, 435.67) * mm});
            skPoint(sketch, "E195.13.8.0", {"position": v(138.22, 441.36) * mm});
            skSolve(sketch);
        }
        {
            var Q0;
            Q0=qCreatedBy(id+"F4.planeOp",FACE);
            var sketch = newSketch(context, id + "F7", { "sketchPlane" : qUnion([Q0])});
            skCircle(sketch, "E196", {"center": v(0, 0) * mm, "radius": 462.5 * mm, "construction": true});
            skLineSegment(sketch, "E197", {"start": v(0, 0) * mm, "end": v(0, 462.5) * mm, "construction": true});
            skPoint(sketch, "E198", {"position": v(0, 737.5) * mm});
            skPoint(sketch, "E199", {"position": v(-110, 692.5) * mm});
            skPoint(sketch, "E200", {"position": v(0, 729.5) * mm});
            skPoint(sketch, "E201", {"position": v(-97, 692.5) * mm});
            skLineSegment(sketch, "E202", {"start": v(0, 0) * mm, "end": v(-172.02, 429.32) * mm, "construction": true});
            skLineSegment(sketch, "E203", {"start": v(-172.02, 429.32) * mm, "end": v(-176.48, 440.46) * mm, "construction": true});
            skPoint(sketch, "E204", {"position": v(-174.25, 434.9) * mm});
            skArc(sketch, "E205", {"start": v(-174.25, 434.9) * mm, "mid": v(-160.23, 440.25) * mm, "end": v(-146.06, 445.15) * mm});
            skArc(sketch, "E206", {"start": v(-176.48, 440.46) * mm, "mid": v(-166.98, 444.15) * mm, "end": v(-157.4, 447.63) * mm});
            skLineSegment(sketch, "E207", {"start": v(-176.48, 440.46) * mm, "end": v(-174.25, 434.9) * mm});
            skLineSegment(sketch, "E208", {"start": v(0, 0) * mm, "end": v(-146.06, 445.15) * mm, "construction": true});
            skLineSegment(sketch, "E209", {"start": v(-146.06, 445.15) * mm, "end": v(-148.66, 453.08) * mm, "construction": true});
            skPoint(sketch, "E210.MirrorP", {"position": v(174.25, 434.9) * mm});
            skLineSegment(sketch, "E211.MirrorCS", {"start": v(146.06, 445.15) * mm, "end": v(148.66, 453.08) * mm, "construction": true});
            skLineSegment(sketch, "E212.MirrorCS", {"start": v(172.02, 429.32) * mm, "end": v(176.48, 440.46) * mm, "construction": true});
            skLineSegment(sketch, "E213.MirrorCS", {"start": v(0, 0) * mm, "end": v(172.02, 429.32) * mm, "construction": true});
            skLineSegment(sketch, "E214.MirrorCS", {"start": v(0, 0) * mm, "end": v(146.06, 445.15) * mm, "construction": true});
            skArc(sketch, "E215", {"start": v(146.06, 445.15) * mm, "mid": v(160.23, 440.25) * mm, "end": v(174.25, 434.9) * mm});
            skLineSegment(sketch, "E216", {"start": v(174.25, 434.9) * mm, "end": v(172.02, 429.32) * mm});
            skPoint(sketch, "E217", {"position": v(131.78, 443.33) * mm});
            skPoint(sketch, "E218", {"position": v(144.19, 439.45) * mm});
            skArc(sketch, "E219", {"start": v(131.78, 443.33) * mm, "mid": v(152.06, 436.79) * mm, "end": v(172.02, 429.32) * mm});
            skLineSegment(sketch, "E220", {"start": v(-157.4, 692.5) * mm, "end": v(-110, 692.5) * mm, "construction": true});
            skPoint(sketch, "E221", {"position": v(-133.7, 692.5) * mm});
            skLineSegment(sketch, "E222", {"start": v(-157.4, 692.5) * mm, "end": v(-157.4, 447.63) * mm, "construction": true});
            skPoint(sketch, "E223", {"position": v(-157.4, 570.07) * mm});
            skPoint(sketch, "E224", {"position": v(-133.7, 570.07) * mm});
            skArc(sketch, "E225", {"start": v(-157.4, 447.63) * mm, "mid": v(-139.68, 507.71) * mm, "end": v(-133.7, 570.07) * mm});
            skArc(sketch, "E226", {"start": v(-110, 692.5) * mm, "mid": v(-127.72, 632.42) * mm, "end": v(-133.7, 570.07) * mm});
            skArc(sketch, "E227", {"start": v(0, 737.5) * mm, "mid": v(-59.42, 725.82) * mm, "end": v(-110, 692.5) * mm});
            skLineSegment(sketch, "E228", {"start": v(0, 737.5) * mm, "end": v(0, 729.5) * mm});
            skArc(sketch, "E229", {"start": v(0, 729.5) * mm, "mid": v(-51.9, 719.94) * mm, "end": v(-97, 692.5) * mm});
            skArc(sketch, "E230", {"start": v(-97, 692.5) * mm, "mid": v(-5.55, 539.27) * mm, "end": v(146.06, 445.15) * mm});
            skArc(sketch, "E231", {"start": v(-146.06, 445.15) * mm, "mid": v(-127.1, 506.34) * mm, "end": v(-120.7, 570.07) * mm});
            skArc(sketch, "E232", {"start": v(-103.63, 668.34) * mm, "mid": v(-116.4, 619.94) * mm, "end": v(-120.7, 570.07) * mm});
            skPoint(sketch, "E233", {"position": v(-118.63, 668.34) * mm});
            skPoint(sketch, "E234", {"position": v(-88.63, 668.34) * mm});
            skLineSegment(sketch, "E235", {"start": v(-118.63, 668.34) * mm, "end": v(-88.63, 668.34) * mm, "construction": true});
            skArc(sketch, "E236", {"start": v(-103.63, 668.34) * mm, "mid": v(-10.1, 530.54) * mm, "end": v(131.78, 443.33) * mm});
            skPoint(sketch, "E237.1.14", {"position": v(-146.06, 445.15) * mm});
            skPoint(sketch, "E237.1.28", {"position": v(-144.2, 439.45) * mm});
            skArc(sketch, "E237.1.30", {"start": v(-184.02, 424.31) * mm, "mid": v(-164.28, 432.34) * mm, "end": v(-144.2, 439.45) * mm});
            skArc(sketch, "E237.1.32", {"start": v(-174.25, 434.89) * mm, "mid": v(-160.24, 440.24) * mm, "end": v(-146.06, 445.15) * mm});
            skLineSegment(sketch, "E237.1.37", {"start": v(-174.25, 434.89) * mm, "end": v(-177.36, 442.64) * mm, "construction": true});
            skLineSegment(sketch, "E237.1.39", {"start": v(-146.06, 445.15) * mm, "end": v(-144.2, 439.45) * mm});
            skLineSegment(sketch, "E237.1.40", {"start": v(-143.86, 438.33) * mm, "end": v(-147.6, 449.73) * mm, "construction": true});
            skPoint(sketch, "E237.8.8", {"position": v(146.06, 448.35) * mm});
            skPoint(sketch, "E237.8.26", {"position": v(144.2, 442.65) * mm});
            skLineSegment(sketch, "E237.8.33", {"start": v(144.2, 442.65) * mm, "end": v(147.93, 454.05) * mm, "construction": true});
            skArc(sketch, "E237.8.35", {"start": v(146.06, 448.35) * mm, "mid": v(160.24, 443.45) * mm, "end": v(174.25, 438.1) * mm});
            skLineSegment(sketch, "E237.8.36", {"start": v(147.93, 454.05) * mm, "end": v(146.06, 448.35) * mm});
            skLineSegment(sketch, "E237.8.38", {"start": v(174.25, 438.1) * mm, "end": v(177.36, 445.84) * mm, "construction": true});
            skArc(sketch, "E238", {"start": v(-144.2, 439.45) * mm, "mid": v(-6.5, 462.45) * mm, "end": v(131.78, 443.33) * mm});
            skPoint(sketch, "E239", {"position": v(-135.64, 442.16) * mm});
            skPoint(sketch, "E240", {"position": v(-127.05, 444.7) * mm});
            skLineSegment(sketch, "E241", {"start": v(-135.64, 442.16) * mm, "end": v(0, 0) * mm, "construction": true});
            skPoint(sketch, "E242", {"position": v(-131.25, 427.82) * mm});
            skArc(sketch, "E243", {"start": v(-131.25, 427.82) * mm, "mid": v(-127.7, 428.89) * mm, "end": v(-124.16, 429.93) * mm, "construction": true});
            skArc(sketch, "E244", {"start": v(-131.25, 427.82) * mm, "mid": v(-135.06, 426.63) * mm, "end": v(-138.87, 425.4) * mm, "construction": true});
            skPoint(sketch, "E245", {"position": v(-127.7, 428.89) * mm});
            skPoint(sketch, "E246", {"position": v(-135.06, 426.63) * mm});
            skLineSegment(sketch, "E247", {"start": v(0, 0) * mm, "end": v(-127.05, 444.7) * mm, "construction": true});
            skLineSegment(sketch, "E248", {"start": v(-127.05, 444.7) * mm, "end": v(-129.19, 452.2) * mm, "construction": true});
            skArc(sketch, "E249", {"start": v(-144.2, 439.45) * mm, "mid": v(-140.77, 432.23) * mm, "end": v(-135.06, 426.63) * mm});
            skArc(sketch, "E250", {"start": v(-127.7, 428.89) * mm, "mid": v(-126.1, 436.75) * mm, "end": v(-127.05, 444.7) * mm});
            skArc(sketch, "E251", {"start": v(-135.06, 426.63) * mm, "mid": v(-131.17, 427.05) * mm, "end": v(-127.7, 428.89) * mm});
            skLineSegment(sketch, "E252.anchor1", {"start": v(0, 0) * mm, "end": v(-135.06, 426.63) * mm, "construction": true});
            skLineSegment(sketch, "E252.anchor2", {"start": v(0, 0) * mm, "end": v(154.76, 419.89) * mm, "construction": true});
            skArc(sketch, "E253", {"start": v(-144.79, 448.2) * mm, "mid": v(-30.76, 470) * mm, "end": v(85.14, 463.24) * mm});
            skPoint(sketch, "E254", {"position": v(163.66, 432.58) * mm});
            skPoint(sketch, "E255", {"position": v(155.24, 435.67) * mm});
            skLineSegment(sketch, "E256", {"start": v(155.24, 435.67) * mm, "end": v(154.15, 432.04) * mm, "construction": true});
            skArc(sketch, "E257.1.0", {"start": v(-109.7, 449.3) * mm, "mid": v(-106.85, 441.83) * mm, "end": v(-101.6, 435.81) * mm});
            skArc(sketch, "E257.1.1", {"start": v(-101.6, 435.81) * mm, "mid": v(-97.68, 435.93) * mm, "end": v(-94.1, 437.5) * mm});
            skArc(sketch, "E257.1.2", {"start": v(-94.1, 437.5) * mm, "mid": v(-91.88, 445.2) * mm, "end": v(-92.2, 453.22) * mm});
            skPoint(sketch, "E257.1.3", {"position": v(-92.2, 453.22) * mm});
            skPoint(sketch, "E257.1.4", {"position": v(-109.7, 449.3) * mm});
            skArc(sketch, "E257.2.0", {"start": v(-74.56, 456.45) * mm, "mid": v(-72.3, 448.79) * mm, "end": v(-67.52, 442.38) * mm});
            skArc(sketch, "E257.2.1", {"start": v(-67.52, 442.38) * mm, "mid": v(-63.6, 442.18) * mm, "end": v(-59.9, 443.47) * mm});
            skArc(sketch, "E257.2.2", {"start": v(-59.9, 443.47) * mm, "mid": v(-57.1, 450.99) * mm, "end": v(-56.8, 459) * mm});
            skPoint(sketch, "E257.2.3", {"position": v(-56.8, 459) * mm});
            skPoint(sketch, "E257.2.4", {"position": v(-74.56, 456.45) * mm});
            skLineSegment(sketch, "E257.anchor2", {"start": v(0, 0) * mm, "end": v(138.2, 425.63) * mm, "construction": true});
            skArc(sketch, "E258.3.3.0", {"start": v(-38.96, 460.86) * mm, "mid": v(-37.3, 453.04) * mm, "end": v(-33.04, 446.28) * mm});
            skArc(sketch, "E258.4.3.0", {"start": v(-33.04, 446.28) * mm, "mid": v(-29.15, 445.78) * mm, "end": v(-25.36, 446.78) * mm});
            skArc(sketch, "E258.8.3.0", {"start": v(-25.36, 446.78) * mm, "mid": v(-21.98, 454.05) * mm, "end": v(-21.07, 462.02) * mm});
            skPoint(sketch, "E258.12.3.0", {"position": v(-21.07, 462.02) * mm});
            skPoint(sketch, "E258.13.3.0", {"position": v(-38.96, 460.86) * mm});
            skArc(sketch, "E258.3.4.0", {"start": v(-3.13, 462.49) * mm, "mid": v(-2.08, 454.57) * mm, "end": v(1.64, 447.5) * mm});
            skArc(sketch, "E258.4.4.0", {"start": v(1.64, 447.5) * mm, "mid": v(5.48, 446.7) * mm, "end": v(9.34, 447.4) * mm});
            skArc(sketch, "E258.8.4.0", {"start": v(9.34, 447.4) * mm, "mid": v(13.27, 454.4) * mm, "end": v(14.8, 462.26) * mm});
            skPoint(sketch, "E258.12.4.0", {"position": v(14.8, 462.26) * mm});
            skPoint(sketch, "E258.13.4.0", {"position": v(-3.13, 462.49) * mm});
            skArc(sketch, "E258.3.5.0", {"start": v(32.72, 461.34) * mm, "mid": v(33.15, 453.36) * mm, "end": v(36.32, 446.02) * mm});
            skArc(sketch, "E258.4.5.0", {"start": v(36.32, 446.02) * mm, "mid": v(40.08, 444.93) * mm, "end": v(43.98, 445.33) * mm});
            skArc(sketch, "E258.8.5.0", {"start": v(43.98, 445.33) * mm, "mid": v(48.44, 452) * mm, "end": v(50.57, 459.73) * mm});
            skPoint(sketch, "E258.12.5.0", {"position": v(50.57, 459.73) * mm});
            skPoint(sketch, "E258.13.5.0", {"position": v(32.72, 461.34) * mm});
            skArc(sketch, "E258.3.6.0", {"start": v(68.37, 457.42) * mm, "mid": v(68.18, 449.43) * mm, "end": v(70.77, 441.87) * mm});
            skArc(sketch, "E258.4.6.0", {"start": v(70.77, 441.87) * mm, "mid": v(74.44, 440.49) * mm, "end": v(78.36, 440.59) * mm});
            skArc(sketch, "E258.8.6.0", {"start": v(78.36, 440.59) * mm, "mid": v(83.32, 446.88) * mm, "end": v(86.05, 454.42) * mm});
            skPoint(sketch, "E258.12.6.0", {"position": v(86.05, 454.42) * mm});
            skPoint(sketch, "E258.13.6.0", {"position": v(68.37, 457.42) * mm});
            skArc(sketch, "E258.3.7.0", {"start": v(103.6, 450.75) * mm, "mid": v(102.8, 442.8) * mm, "end": v(104.8, 435.06) * mm});
            skArc(sketch, "E258.4.7.0", {"start": v(104.8, 435.06) * mm, "mid": v(108.35, 433.4) * mm, "end": v(112.26, 433.19) * mm});
            skArc(sketch, "E258.8.7.0", {"start": v(112.26, 433.19) * mm, "mid": v(117.7, 439.08) * mm, "end": v(121, 446.4) * mm});
            skPoint(sketch, "E258.12.7.0", {"position": v(121, 446.4) * mm});
            skPoint(sketch, "E258.13.7.0", {"position": v(103.6, 450.75) * mm});
            skArc(sketch, "E258.3.8.0", {"start": v(138.22, 441.36) * mm, "mid": v(136.8, 433.5) * mm, "end": v(138.2, 425.63) * mm});
            skArc(sketch, "E258.4.8.0", {"start": v(138.2, 425.63) * mm, "mid": v(141.6, 423.7) * mm, "end": v(145.5, 423.19) * mm});
            skArc(sketch, "E258.8.8.0", {"start": v(145.5, 423.19) * mm, "mid": v(151.37, 428.64) * mm, "end": v(155.23, 435.67) * mm});
            skPoint(sketch, "E258.12.8.0", {"position": v(155.23, 435.67) * mm});
            skPoint(sketch, "E258.13.8.0", {"position": v(138.22, 441.36) * mm});
            skSolve(sketch);
        }
        {
            var Q0;
            Q0=qCreatedBy(id+"F2.planeOp",FACE);
            var sketch = newSketch(context, id + "F8", { "sketchPlane" : qUnion([Q0])});
            skCircle(sketch, "E259", {"center": v(0, 0) * mm, "radius": 462.5 * mm, "construction": true});
            skLineSegment(sketch, "E260", {"start": v(0, 0) * mm, "end": v(0, 462.5) * mm, "construction": true});
            skPoint(sketch, "E261", {"position": v(0, 737.5) * mm});
            skPoint(sketch, "E262", {"position": v(-110, 692.5) * mm});
            skPoint(sketch, "E263", {"position": v(0, 729.5) * mm});
            skPoint(sketch, "E264", {"position": v(-97, 692.5) * mm});
            skLineSegment(sketch, "E265", {"start": v(0, 0) * mm, "end": v(-172.02, 429.32) * mm, "construction": true});
            skLineSegment(sketch, "E266", {"start": v(-172.02, 429.32) * mm, "end": v(-176.48, 440.46) * mm, "construction": true});
            skPoint(sketch, "E267", {"position": v(-174.25, 434.9) * mm});
            skArc(sketch, "E268", {"start": v(-174.25, 434.9) * mm, "mid": v(-160.23, 440.25) * mm, "end": v(-146.06, 445.15) * mm});
            skArc(sketch, "E269", {"start": v(-176.48, 440.46) * mm, "mid": v(-166.98, 444.15) * mm, "end": v(-157.4, 447.63) * mm});
            skLineSegment(sketch, "E270", {"start": v(-176.48, 440.46) * mm, "end": v(-174.25, 434.9) * mm});
            skLineSegment(sketch, "E271", {"start": v(0, 0) * mm, "end": v(-146.06, 445.15) * mm, "construction": true});
            skLineSegment(sketch, "E272", {"start": v(-146.06, 445.15) * mm, "end": v(-148.66, 453.08) * mm, "construction": true});
            skPoint(sketch, "E273.MirrorP", {"position": v(174.25, 434.9) * mm});
            skLineSegment(sketch, "E274.MirrorCS", {"start": v(146.06, 445.15) * mm, "end": v(148.66, 453.08) * mm, "construction": true});
            skLineSegment(sketch, "E275.MirrorCS", {"start": v(172.02, 429.32) * mm, "end": v(176.48, 440.46) * mm, "construction": true});
            skLineSegment(sketch, "E276.MirrorCS", {"start": v(0, 0) * mm, "end": v(172.02, 429.32) * mm, "construction": true});
            skLineSegment(sketch, "E277.MirrorCS", {"start": v(0, 0) * mm, "end": v(146.06, 445.15) * mm, "construction": true});
            skArc(sketch, "E278", {"start": v(146.06, 445.15) * mm, "mid": v(160.23, 440.25) * mm, "end": v(174.25, 434.9) * mm});
            skLineSegment(sketch, "E279", {"start": v(174.25, 434.9) * mm, "end": v(172.02, 429.32) * mm});
            skPoint(sketch, "E280", {"position": v(131.78, 443.33) * mm});
            skPoint(sketch, "E281", {"position": v(144.19, 439.45) * mm});
            skArc(sketch, "E282", {"start": v(131.78, 443.33) * mm, "mid": v(152.06, 436.79) * mm, "end": v(172.02, 429.32) * mm});
            skLineSegment(sketch, "E283", {"start": v(-157.4, 692.5) * mm, "end": v(-110, 692.5) * mm, "construction": true});
            skPoint(sketch, "E284", {"position": v(-133.7, 692.5) * mm});
            skLineSegment(sketch, "E285", {"start": v(-157.4, 692.5) * mm, "end": v(-157.4, 447.63) * mm, "construction": true});
            skPoint(sketch, "E286", {"position": v(-157.4, 570.07) * mm});
            skPoint(sketch, "E287", {"position": v(-133.7, 570.07) * mm});
            skArc(sketch, "E288", {"start": v(-157.4, 447.63) * mm, "mid": v(-139.68, 507.71) * mm, "end": v(-133.7, 570.07) * mm});
            skArc(sketch, "E289", {"start": v(-110, 692.5) * mm, "mid": v(-127.72, 632.42) * mm, "end": v(-133.7, 570.07) * mm});
            skArc(sketch, "E290", {"start": v(0, 737.5) * mm, "mid": v(-59.42, 725.82) * mm, "end": v(-110, 692.5) * mm});
            skLineSegment(sketch, "E291", {"start": v(0, 737.5) * mm, "end": v(0, 729.5) * mm});
            skArc(sketch, "E292", {"start": v(0, 729.5) * mm, "mid": v(-51.9, 719.94) * mm, "end": v(-97, 692.5) * mm});
            skArc(sketch, "E293", {"start": v(-97, 692.5) * mm, "mid": v(-5.55, 539.27) * mm, "end": v(146.06, 445.15) * mm});
            skArc(sketch, "E294", {"start": v(-146.06, 445.15) * mm, "mid": v(-127.1, 506.34) * mm, "end": v(-120.7, 570.07) * mm});
            skArc(sketch, "E295", {"start": v(-103.63, 668.34) * mm, "mid": v(-116.4, 619.94) * mm, "end": v(-120.7, 570.07) * mm});
            skPoint(sketch, "E296", {"position": v(-118.63, 668.34) * mm});
            skPoint(sketch, "E297", {"position": v(-88.63, 668.34) * mm});
            skLineSegment(sketch, "E298", {"start": v(-118.63, 668.34) * mm, "end": v(-88.63, 668.34) * mm, "construction": true});
            skArc(sketch, "E299", {"start": v(-103.63, 668.34) * mm, "mid": v(-10.1, 530.54) * mm, "end": v(131.78, 443.33) * mm});
            skPoint(sketch, "E300.1.14", {"position": v(-146.06, 445.15) * mm});
            skPoint(sketch, "E300.1.28", {"position": v(-144.2, 439.45) * mm});
            skArc(sketch, "E300.1.30", {"start": v(-184.02, 424.31) * mm, "mid": v(-164.28, 432.34) * mm, "end": v(-144.2, 439.45) * mm});
            skArc(sketch, "E300.1.32", {"start": v(-174.25, 434.89) * mm, "mid": v(-160.24, 440.24) * mm, "end": v(-146.06, 445.15) * mm});
            skLineSegment(sketch, "E300.1.37", {"start": v(-174.25, 434.89) * mm, "end": v(-177.36, 442.64) * mm, "construction": true});
            skLineSegment(sketch, "E300.1.39", {"start": v(-146.06, 445.15) * mm, "end": v(-144.2, 439.45) * mm});
            skLineSegment(sketch, "E300.1.40", {"start": v(-143.86, 438.33) * mm, "end": v(-147.6, 449.73) * mm, "construction": true});
            skPoint(sketch, "E300.8.8", {"position": v(146.06, 448.35) * mm});
            skPoint(sketch, "E300.8.26", {"position": v(144.2, 442.65) * mm});
            skLineSegment(sketch, "E300.8.33", {"start": v(144.2, 442.65) * mm, "end": v(147.93, 454.05) * mm, "construction": true});
            skArc(sketch, "E300.8.35", {"start": v(146.06, 448.35) * mm, "mid": v(160.24, 443.45) * mm, "end": v(174.25, 438.1) * mm});
            skLineSegment(sketch, "E300.8.36", {"start": v(147.93, 454.05) * mm, "end": v(146.06, 448.35) * mm});
            skLineSegment(sketch, "E300.8.38", {"start": v(174.25, 438.1) * mm, "end": v(177.36, 445.84) * mm, "construction": true});
            skArc(sketch, "E301", {"start": v(-144.2, 439.45) * mm, "mid": v(-6.5, 462.45) * mm, "end": v(131.78, 443.33) * mm});
            skPoint(sketch, "E302", {"position": v(-135.64, 442.16) * mm});
            skPoint(sketch, "E303", {"position": v(-127.05, 444.7) * mm});
            skLineSegment(sketch, "E304", {"start": v(-135.64, 442.16) * mm, "end": v(0, 0) * mm, "construction": true});
            skPoint(sketch, "E305", {"position": v(-131.25, 427.82) * mm});
            skArc(sketch, "E306", {"start": v(-131.25, 427.82) * mm, "mid": v(-127.7, 428.89) * mm, "end": v(-124.16, 429.93) * mm, "construction": true});
            skArc(sketch, "E307", {"start": v(-131.25, 427.82) * mm, "mid": v(-135.06, 426.63) * mm, "end": v(-138.87, 425.4) * mm, "construction": true});
            skPoint(sketch, "E308", {"position": v(-127.7, 428.89) * mm});
            skPoint(sketch, "E309", {"position": v(-135.06, 426.63) * mm});
            skLineSegment(sketch, "E310", {"start": v(0, 0) * mm, "end": v(-127.05, 444.7) * mm, "construction": true});
            skLineSegment(sketch, "E311", {"start": v(-127.05, 444.7) * mm, "end": v(-129.19, 452.2) * mm, "construction": true});
            skArc(sketch, "E312", {"start": v(-144.2, 439.45) * mm, "mid": v(-140.77, 432.23) * mm, "end": v(-135.06, 426.63) * mm});
            skArc(sketch, "E313", {"start": v(-127.7, 428.89) * mm, "mid": v(-126.1, 436.75) * mm, "end": v(-127.05, 444.7) * mm});
            skArc(sketch, "E314", {"start": v(-135.06, 426.63) * mm, "mid": v(-131.17, 427.05) * mm, "end": v(-127.7, 428.89) * mm});
            skLineSegment(sketch, "E315.anchor1", {"start": v(0, 0) * mm, "end": v(-135.06, 426.63) * mm, "construction": true});
            skLineSegment(sketch, "E315.anchor2", {"start": v(0, 0) * mm, "end": v(154.76, 419.89) * mm, "construction": true});
            skArc(sketch, "E316", {"start": v(-144.79, 448.2) * mm, "mid": v(-30.76, 470) * mm, "end": v(85.14, 463.24) * mm});
            skPoint(sketch, "E317", {"position": v(163.66, 432.58) * mm});
            skPoint(sketch, "E318", {"position": v(155.24, 435.67) * mm});
            skLineSegment(sketch, "E319", {"start": v(155.24, 435.67) * mm, "end": v(154.15, 432.04) * mm, "construction": true});
            skArc(sketch, "E320.1.0", {"start": v(-109.7, 449.3) * mm, "mid": v(-106.85, 441.83) * mm, "end": v(-101.6, 435.81) * mm});
            skArc(sketch, "E320.1.1", {"start": v(-101.6, 435.81) * mm, "mid": v(-97.68, 435.93) * mm, "end": v(-94.1, 437.5) * mm});
            skArc(sketch, "E320.1.2", {"start": v(-94.1, 437.5) * mm, "mid": v(-91.88, 445.2) * mm, "end": v(-92.2, 453.22) * mm});
            skPoint(sketch, "E320.1.3", {"position": v(-92.2, 453.22) * mm});
            skPoint(sketch, "E320.1.4", {"position": v(-109.7, 449.3) * mm});
            skArc(sketch, "E320.2.0", {"start": v(-74.56, 456.45) * mm, "mid": v(-72.3, 448.79) * mm, "end": v(-67.52, 442.38) * mm});
            skArc(sketch, "E320.2.1", {"start": v(-67.52, 442.38) * mm, "mid": v(-63.6, 442.18) * mm, "end": v(-59.9, 443.47) * mm});
            skArc(sketch, "E320.2.2", {"start": v(-59.9, 443.47) * mm, "mid": v(-57.1, 450.99) * mm, "end": v(-56.8, 459) * mm});
            skPoint(sketch, "E320.2.3", {"position": v(-56.8, 459) * mm});
            skPoint(sketch, "E320.2.4", {"position": v(-74.56, 456.45) * mm});
            skLineSegment(sketch, "E320.anchor2", {"start": v(0, 0) * mm, "end": v(138.2, 425.63) * mm, "construction": true});
            skArc(sketch, "E321.3.3.0", {"start": v(-38.96, 460.86) * mm, "mid": v(-37.3, 453.04) * mm, "end": v(-33.04, 446.28) * mm});
            skArc(sketch, "E321.4.3.0", {"start": v(-33.04, 446.28) * mm, "mid": v(-29.15, 445.78) * mm, "end": v(-25.36, 446.78) * mm});
            skArc(sketch, "E321.8.3.0", {"start": v(-25.36, 446.78) * mm, "mid": v(-21.98, 454.05) * mm, "end": v(-21.07, 462.02) * mm});
            skPoint(sketch, "E321.12.3.0", {"position": v(-21.07, 462.02) * mm});
            skPoint(sketch, "E321.13.3.0", {"position": v(-38.96, 460.86) * mm});
            skArc(sketch, "E321.3.4.0", {"start": v(-3.13, 462.49) * mm, "mid": v(-2.08, 454.57) * mm, "end": v(1.64, 447.5) * mm});
            skArc(sketch, "E321.4.4.0", {"start": v(1.64, 447.5) * mm, "mid": v(5.48, 446.7) * mm, "end": v(9.34, 447.4) * mm});
            skArc(sketch, "E321.8.4.0", {"start": v(9.34, 447.4) * mm, "mid": v(13.27, 454.4) * mm, "end": v(14.8, 462.26) * mm});
            skPoint(sketch, "E321.12.4.0", {"position": v(14.8, 462.26) * mm});
            skPoint(sketch, "E321.13.4.0", {"position": v(-3.13, 462.49) * mm});
            skArc(sketch, "E321.3.5.0", {"start": v(32.72, 461.34) * mm, "mid": v(33.15, 453.36) * mm, "end": v(36.32, 446.02) * mm});
            skArc(sketch, "E321.4.5.0", {"start": v(36.32, 446.02) * mm, "mid": v(40.08, 444.93) * mm, "end": v(43.98, 445.33) * mm});
            skArc(sketch, "E321.8.5.0", {"start": v(43.98, 445.33) * mm, "mid": v(48.44, 452) * mm, "end": v(50.57, 459.73) * mm});
            skPoint(sketch, "E321.12.5.0", {"position": v(50.57, 459.73) * mm});
            skPoint(sketch, "E321.13.5.0", {"position": v(32.72, 461.34) * mm});
            skArc(sketch, "E321.3.6.0", {"start": v(68.37, 457.42) * mm, "mid": v(68.18, 449.43) * mm, "end": v(70.77, 441.87) * mm});
            skArc(sketch, "E321.4.6.0", {"start": v(70.77, 441.87) * mm, "mid": v(74.44, 440.49) * mm, "end": v(78.36, 440.59) * mm});
            skArc(sketch, "E321.8.6.0", {"start": v(78.36, 440.59) * mm, "mid": v(83.32, 446.88) * mm, "end": v(86.05, 454.42) * mm});
            skPoint(sketch, "E321.12.6.0", {"position": v(86.05, 454.42) * mm});
            skPoint(sketch, "E321.13.6.0", {"position": v(68.37, 457.42) * mm});
            skArc(sketch, "E321.3.7.0", {"start": v(103.6, 450.75) * mm, "mid": v(102.8, 442.8) * mm, "end": v(104.8, 435.06) * mm});
            skArc(sketch, "E321.4.7.0", {"start": v(104.8, 435.06) * mm, "mid": v(108.35, 433.4) * mm, "end": v(112.26, 433.19) * mm});
            skArc(sketch, "E321.8.7.0", {"start": v(112.26, 433.19) * mm, "mid": v(117.7, 439.08) * mm, "end": v(121, 446.4) * mm});
            skPoint(sketch, "E321.12.7.0", {"position": v(121, 446.4) * mm});
            skPoint(sketch, "E321.13.7.0", {"position": v(103.6, 450.75) * mm});
            skArc(sketch, "E321.3.8.0", {"start": v(138.22, 441.36) * mm, "mid": v(136.8, 433.5) * mm, "end": v(138.2, 425.63) * mm});
            skArc(sketch, "E321.4.8.0", {"start": v(138.2, 425.63) * mm, "mid": v(141.6, 423.7) * mm, "end": v(145.5, 423.19) * mm});
            skArc(sketch, "E321.8.8.0", {"start": v(145.5, 423.19) * mm, "mid": v(151.37, 428.64) * mm, "end": v(155.23, 435.67) * mm});
            skPoint(sketch, "E321.12.8.0", {"position": v(155.23, 435.67) * mm});
            skPoint(sketch, "E321.13.8.0", {"position": v(138.22, 441.36) * mm});
            skSolve(sketch);
        }
        {
            var Q0;
            {var subQ6=sQuery(id+"F5.wireOp",EDGE,"E79");Q0=makeQuery(id+"F5.imprint","IMPRINT",FACE,{"disambiguationData":[TD([[makeQuery(id+"F5.imprint","IMPRINT",EDGE,{"derivedFrom":subQ6}),-1.0]])]});}
            extrude(context, id + "F9", {"entities" : qUnion([Q0]), "operationType" : NewBodyOperationType.ADD, "depth" : 30 * mm});
        }
        {
            var Q0;
            {var subQ6=sQuery(id+"F6.wireOp",EDGE,"E142");Q0=makeQuery(id+"F6.imprint","IMPRINT",FACE,{"disambiguationData":[TD([[makeQuery(id+"F6.imprint","IMPRINT",EDGE,{"derivedFrom":subQ6}),-1.0]])]});}
            extrude(context, id + "F10", {"entities" : qUnion([Q0]), "operationType" : NewBodyOperationType.ADD, "depth" : 15 * mm, "hasSecondDirection" : true, "secondDirectionOppositeDirection" : true, "secondDirectionDepth" : 15 * mm});
        }
        {
            var Q0;
            {var subQ6=sQuery(id+"F7.wireOp",EDGE,"E205");Q0=makeQuery(id+"F7.imprint","IMPRINT",FACE,{"disambiguationData":[TD([[makeQuery(id+"F7.imprint","IMPRINT",EDGE,{"derivedFrom":subQ6}),-1.0]])]});}
            extrude(context, id + "F11", {"entities" : qUnion([Q0]), "operationType" : NewBodyOperationType.ADD, "depth" : 15 * mm, "hasSecondDirection" : true, "secondDirectionOppositeDirection" : true, "secondDirectionDepth" : 15 * mm});
        }
        {
            var Q0;
            {var subQ6=sQuery(id+"F8.wireOp",EDGE,"E268");Q0=makeQuery(id+"F8.imprint","IMPRINT",FACE,{"disambiguationData":[TD([[makeQuery(id+"F8.imprint","IMPRINT",EDGE,{"derivedFrom":subQ6}),-1.0]])]});}
            extrude(context, id + "F12", {"entities" : qUnion([Q0]), "operationType" : NewBodyOperationType.ADD, "oppositeDirection" : true, "depth" : 30 * mm});
        }
        {
            var Q0;
            {var subQ0=sQuery(id+"F5.wireOp",EDGE,"E106");Q0=makeQuery(id+"F5.imprint","IMPRINT",FACE,{"disambiguationData":[TD([[makeQuery(id+"F5.imprint","IMPRINT",EDGE,{"derivedFrom":subQ0}),1.0]])]});}
            extrude(context, id + "F13", {"entities" : qUnion([Q0]), "operationType" : NewBodyOperationType.ADD, "depth" : 10 * mm});
        }
        {
            var Q0;
            {var subQ0=sQuery(id+"F6.wireOp",EDGE,"E169");Q0=makeQuery(id+"F6.imprint","IMPRINT",FACE,{"disambiguationData":[TD([[makeQuery(id+"F6.imprint","IMPRINT",EDGE,{"derivedFrom":subQ0}),1.0]])]});}
            extrude(context, id + "F14", {"entities" : qUnion([Q0]), "operationType" : NewBodyOperationType.ADD, "depth" : 5 * mm, "hasSecondDirection" : true, "secondDirectionOppositeDirection" : true, "secondDirectionDepth" : 5 * mm});
        }
        {
            var Q0;
            {var subQ0=sQuery(id+"F7.wireOp",EDGE,"E232");Q0=makeQuery(id+"F7.imprint","IMPRINT",FACE,{"disambiguationData":[TD([[makeQuery(id+"F7.imprint","IMPRINT",EDGE,{"derivedFrom":subQ0}),1.0]])]});}
            extrude(context, id + "F15", {"entities" : qUnion([Q0]), "operationType" : NewBodyOperationType.ADD, "depth" : 5 * mm, "hasSecondDirection" : true, "secondDirectionOppositeDirection" : true, "secondDirectionDepth" : 5 * mm});
        }
        {
            var Q0;
            {var subQ0=sQuery(id+"F8.wireOp",EDGE,"E295");Q0=makeQuery(id+"F8.imprint","IMPRINT",FACE,{"disambiguationData":[TD([[makeQuery(id+"F8.imprint","IMPRINT",EDGE,{"derivedFrom":subQ0}),1.0]])]});}
            extrude(context, id + "F16", {"entities" : qUnion([Q0]), "operationType" : NewBodyOperationType.ADD, "oppositeDirection" : true, "depth" : 10 * mm});
        }
        {
            var Q0;
            Q0=qCreatedBy(makeId("Front.planeOp"),FACE);
            cPlane(context, id + "F17", {"entities" : qUnion([Q0]), "cplaneType" : CPlaneType.OFFSET, "offset" : 2420 * mm, "width" : 150 * mm, "height" : 150 * mm});
        }
        {
            var Q0;
            Q0=qCreatedBy(id+"F17.planeOp",FACE);
            var sketch = newSketch(context, id + "F18", { "sketchPlane" : qUnion([Q0])});
            skCircle(sketch, "E322", {"center": v(0, 0) * mm, "radius": 462.5 * mm, "construction": true});
            skLineSegment(sketch, "E323", {"start": v(0, 0) * mm, "end": v(0, 462.5) * mm, "construction": true});
            skPoint(sketch, "E324", {"position": v(0, 737.5) * mm});
            skPoint(sketch, "E325", {"position": v(-110, 692.5) * mm});
            skPoint(sketch, "E326", {"position": v(0, 729.5) * mm});
            skPoint(sketch, "E327", {"position": v(-97, 692.5) * mm});
            skLineSegment(sketch, "E328", {"start": v(0, 0) * mm, "end": v(-172.02, 429.32) * mm, "construction": true});
            skLineSegment(sketch, "E329", {"start": v(-172.02, 429.32) * mm, "end": v(-176.48, 440.46) * mm, "construction": true});
            skPoint(sketch, "E330", {"position": v(-174.25, 434.9) * mm});
            skArc(sketch, "E331", {"start": v(-174.25, 434.9) * mm, "mid": v(-160.23, 440.25) * mm, "end": v(-146.06, 445.15) * mm});
            skArc(sketch, "E332", {"start": v(-176.48, 440.46) * mm, "mid": v(-166.98, 444.15) * mm, "end": v(-157.4, 447.63) * mm});
            skLineSegment(sketch, "E333", {"start": v(-176.48, 440.46) * mm, "end": v(-174.25, 434.9) * mm});
            skLineSegment(sketch, "E334", {"start": v(0, 0) * mm, "end": v(-146.06, 445.15) * mm, "construction": true});
            skLineSegment(sketch, "E335", {"start": v(-146.06, 445.15) * mm, "end": v(-148.66, 453.08) * mm, "construction": true});
            skPoint(sketch, "E336.MirrorP", {"position": v(174.25, 434.9) * mm});
            skLineSegment(sketch, "E337.MirrorCS", {"start": v(146.06, 445.15) * mm, "end": v(148.66, 453.08) * mm, "construction": true});
            skLineSegment(sketch, "E338.MirrorCS", {"start": v(172.02, 429.32) * mm, "end": v(176.48, 440.46) * mm, "construction": true});
            skLineSegment(sketch, "E339.MirrorCS", {"start": v(0, 0) * mm, "end": v(172.02, 429.32) * mm, "construction": true});
            skLineSegment(sketch, "E340.MirrorCS", {"start": v(0, 0) * mm, "end": v(146.06, 445.15) * mm, "construction": true});
            skArc(sketch, "E341", {"start": v(146.06, 445.15) * mm, "mid": v(160.23, 440.25) * mm, "end": v(174.25, 434.9) * mm});
            skLineSegment(sketch, "E342", {"start": v(174.25, 434.9) * mm, "end": v(172.02, 429.32) * mm});
            skPoint(sketch, "E343", {"position": v(131.78, 443.33) * mm});
            skPoint(sketch, "E344", {"position": v(144.19, 439.45) * mm});
            skArc(sketch, "E345", {"start": v(131.78, 443.33) * mm, "mid": v(152.06, 436.79) * mm, "end": v(172.02, 429.32) * mm});
            skLineSegment(sketch, "E346", {"start": v(-157.4, 692.5) * mm, "end": v(-110, 692.5) * mm, "construction": true});
            skPoint(sketch, "E347", {"position": v(-133.7, 692.5) * mm});
            skLineSegment(sketch, "E348", {"start": v(-157.4, 692.5) * mm, "end": v(-157.4, 447.63) * mm, "construction": true});
            skPoint(sketch, "E349", {"position": v(-157.4, 570.07) * mm});
            skPoint(sketch, "E350", {"position": v(-133.7, 570.07) * mm});
            skArc(sketch, "E351", {"start": v(-157.4, 447.63) * mm, "mid": v(-139.68, 507.71) * mm, "end": v(-133.7, 570.07) * mm});
            skArc(sketch, "E352", {"start": v(-110, 692.5) * mm, "mid": v(-127.72, 632.42) * mm, "end": v(-133.7, 570.07) * mm});
            skArc(sketch, "E353", {"start": v(0, 737.5) * mm, "mid": v(-59.42, 725.82) * mm, "end": v(-110, 692.5) * mm});
            skLineSegment(sketch, "E354", {"start": v(0, 737.5) * mm, "end": v(0, 729.5) * mm});
            skArc(sketch, "E355", {"start": v(0, 729.5) * mm, "mid": v(-51.9, 719.94) * mm, "end": v(-97, 692.5) * mm});
            skArc(sketch, "E356", {"start": v(-97, 692.5) * mm, "mid": v(-5.55, 539.27) * mm, "end": v(146.06, 445.15) * mm});
            skArc(sketch, "E357", {"start": v(-146.06, 445.15) * mm, "mid": v(-127.1, 506.34) * mm, "end": v(-120.7, 570.07) * mm});
            skArc(sketch, "E358", {"start": v(-103.63, 668.34) * mm, "mid": v(-116.4, 619.94) * mm, "end": v(-120.7, 570.07) * mm});
            skPoint(sketch, "E359", {"position": v(-118.63, 668.34) * mm});
            skPoint(sketch, "E360", {"position": v(-88.63, 668.34) * mm});
            skLineSegment(sketch, "E361", {"start": v(-118.63, 668.34) * mm, "end": v(-88.63, 668.34) * mm, "construction": true});
            skArc(sketch, "E362", {"start": v(-103.63, 668.34) * mm, "mid": v(-10.1, 530.54) * mm, "end": v(131.78, 443.33) * mm});
            skPoint(sketch, "E363.1.14", {"position": v(-146.06, 445.15) * mm});
            skPoint(sketch, "E363.1.28", {"position": v(-144.2, 439.45) * mm});
            skArc(sketch, "E363.1.30", {"start": v(-184.02, 424.31) * mm, "mid": v(-164.28, 432.34) * mm, "end": v(-144.2, 439.45) * mm});
            skArc(sketch, "E363.1.32", {"start": v(-174.25, 434.89) * mm, "mid": v(-160.24, 440.24) * mm, "end": v(-146.06, 445.15) * mm});
            skLineSegment(sketch, "E363.1.37", {"start": v(-174.25, 434.89) * mm, "end": v(-177.36, 442.64) * mm, "construction": true});
            skLineSegment(sketch, "E363.1.39", {"start": v(-146.06, 445.15) * mm, "end": v(-144.2, 439.45) * mm});
            skLineSegment(sketch, "E363.1.40", {"start": v(-143.86, 438.33) * mm, "end": v(-147.6, 449.73) * mm, "construction": true});
            skPoint(sketch, "E363.8.8", {"position": v(146.06, 448.35) * mm});
            skPoint(sketch, "E363.8.26", {"position": v(144.2, 442.65) * mm});
            skLineSegment(sketch, "E363.8.33", {"start": v(144.2, 442.65) * mm, "end": v(147.93, 454.05) * mm, "construction": true});
            skArc(sketch, "E363.8.35", {"start": v(146.06, 448.35) * mm, "mid": v(160.24, 443.45) * mm, "end": v(174.25, 438.1) * mm});
            skLineSegment(sketch, "E363.8.36", {"start": v(147.93, 454.05) * mm, "end": v(146.06, 448.35) * mm});
            skLineSegment(sketch, "E363.8.38", {"start": v(174.25, 438.1) * mm, "end": v(177.36, 445.84) * mm, "construction": true});
            skArc(sketch, "E364", {"start": v(-144.2, 439.45) * mm, "mid": v(-6.5, 462.45) * mm, "end": v(131.78, 443.33) * mm});
            skPoint(sketch, "E365", {"position": v(-135.64, 442.16) * mm});
            skPoint(sketch, "E366", {"position": v(-127.05, 444.7) * mm});
            skLineSegment(sketch, "E367", {"start": v(-135.64, 442.16) * mm, "end": v(0, 0) * mm, "construction": true});
            skPoint(sketch, "E368", {"position": v(-131.25, 427.82) * mm});
            skArc(sketch, "E369", {"start": v(-131.25, 427.82) * mm, "mid": v(-127.7, 428.89) * mm, "end": v(-124.16, 429.93) * mm, "construction": true});
            skArc(sketch, "E370", {"start": v(-131.25, 427.82) * mm, "mid": v(-135.06, 426.63) * mm, "end": v(-138.87, 425.4) * mm, "construction": true});
            skPoint(sketch, "E371", {"position": v(-127.7, 428.89) * mm});
            skPoint(sketch, "E372", {"position": v(-135.06, 426.63) * mm});
            skLineSegment(sketch, "E373", {"start": v(0, 0) * mm, "end": v(-127.05, 444.7) * mm, "construction": true});
            skLineSegment(sketch, "E374", {"start": v(-127.05, 444.7) * mm, "end": v(-129.19, 452.2) * mm, "construction": true});
            skArc(sketch, "E375", {"start": v(-144.2, 439.45) * mm, "mid": v(-140.77, 432.23) * mm, "end": v(-135.06, 426.63) * mm});
            skArc(sketch, "E376", {"start": v(-127.7, 428.89) * mm, "mid": v(-126.1, 436.75) * mm, "end": v(-127.05, 444.7) * mm});
            skArc(sketch, "E377", {"start": v(-135.06, 426.63) * mm, "mid": v(-131.17, 427.05) * mm, "end": v(-127.7, 428.89) * mm});
            skLineSegment(sketch, "E378.anchor1", {"start": v(0, 0) * mm, "end": v(-135.06, 426.63) * mm, "construction": true});
            skLineSegment(sketch, "E378.anchor2", {"start": v(0, 0) * mm, "end": v(154.76, 419.89) * mm, "construction": true});
            skArc(sketch, "E379", {"start": v(-144.79, 448.2) * mm, "mid": v(-30.76, 470) * mm, "end": v(85.14, 463.24) * mm});
            skPoint(sketch, "E380", {"position": v(163.66, 432.58) * mm});
            skPoint(sketch, "E381", {"position": v(155.24, 435.67) * mm});
            skLineSegment(sketch, "E382", {"start": v(155.24, 435.67) * mm, "end": v(154.15, 432.04) * mm, "construction": true});
            skArc(sketch, "E383.1.0", {"start": v(-109.7, 449.3) * mm, "mid": v(-106.85, 441.83) * mm, "end": v(-101.6, 435.81) * mm});
            skArc(sketch, "E383.1.1", {"start": v(-101.6, 435.81) * mm, "mid": v(-97.68, 435.93) * mm, "end": v(-94.1, 437.5) * mm});
            skArc(sketch, "E383.1.2", {"start": v(-94.1, 437.5) * mm, "mid": v(-91.88, 445.2) * mm, "end": v(-92.2, 453.22) * mm});
            skPoint(sketch, "E383.1.3", {"position": v(-92.2, 453.22) * mm});
            skPoint(sketch, "E383.1.4", {"position": v(-109.7, 449.3) * mm});
            skArc(sketch, "E383.2.0", {"start": v(-74.56, 456.45) * mm, "mid": v(-72.3, 448.79) * mm, "end": v(-67.52, 442.38) * mm});
            skArc(sketch, "E383.2.1", {"start": v(-67.52, 442.38) * mm, "mid": v(-63.6, 442.18) * mm, "end": v(-59.9, 443.47) * mm});
            skArc(sketch, "E383.2.2", {"start": v(-59.9, 443.47) * mm, "mid": v(-57.1, 450.99) * mm, "end": v(-56.8, 459) * mm});
            skPoint(sketch, "E383.2.3", {"position": v(-56.8, 459) * mm});
            skPoint(sketch, "E383.2.4", {"position": v(-74.56, 456.45) * mm});
            skLineSegment(sketch, "E383.anchor2", {"start": v(0, 0) * mm, "end": v(138.2, 425.63) * mm, "construction": true});
            skArc(sketch, "E384.3.3.0", {"start": v(-38.96, 460.86) * mm, "mid": v(-37.3, 453.04) * mm, "end": v(-33.04, 446.28) * mm});
            skArc(sketch, "E384.4.3.0", {"start": v(-33.04, 446.28) * mm, "mid": v(-29.15, 445.78) * mm, "end": v(-25.36, 446.78) * mm});
            skArc(sketch, "E384.8.3.0", {"start": v(-25.36, 446.78) * mm, "mid": v(-21.98, 454.05) * mm, "end": v(-21.07, 462.02) * mm});
            skPoint(sketch, "E384.12.3.0", {"position": v(-21.07, 462.02) * mm});
            skPoint(sketch, "E384.13.3.0", {"position": v(-38.96, 460.86) * mm});
            skArc(sketch, "E384.3.4.0", {"start": v(-3.13, 462.49) * mm, "mid": v(-2.08, 454.57) * mm, "end": v(1.64, 447.5) * mm});
            skArc(sketch, "E384.4.4.0", {"start": v(1.64, 447.5) * mm, "mid": v(5.48, 446.7) * mm, "end": v(9.34, 447.4) * mm});
            skArc(sketch, "E384.8.4.0", {"start": v(9.34, 447.4) * mm, "mid": v(13.27, 454.4) * mm, "end": v(14.8, 462.26) * mm});
            skPoint(sketch, "E384.12.4.0", {"position": v(14.8, 462.26) * mm});
            skPoint(sketch, "E384.13.4.0", {"position": v(-3.13, 462.49) * mm});
            skArc(sketch, "E384.3.5.0", {"start": v(32.72, 461.34) * mm, "mid": v(33.15, 453.36) * mm, "end": v(36.32, 446.02) * mm});
            skArc(sketch, "E384.4.5.0", {"start": v(36.32, 446.02) * mm, "mid": v(40.08, 444.93) * mm, "end": v(43.98, 445.33) * mm});
            skArc(sketch, "E384.8.5.0", {"start": v(43.98, 445.33) * mm, "mid": v(48.44, 452) * mm, "end": v(50.57, 459.73) * mm});
            skPoint(sketch, "E384.12.5.0", {"position": v(50.57, 459.73) * mm});
            skPoint(sketch, "E384.13.5.0", {"position": v(32.72, 461.34) * mm});
            skArc(sketch, "E384.3.6.0", {"start": v(68.37, 457.42) * mm, "mid": v(68.18, 449.43) * mm, "end": v(70.77, 441.87) * mm});
            skArc(sketch, "E384.4.6.0", {"start": v(70.77, 441.87) * mm, "mid": v(74.44, 440.49) * mm, "end": v(78.36, 440.59) * mm});
            skArc(sketch, "E384.8.6.0", {"start": v(78.36, 440.59) * mm, "mid": v(83.32, 446.88) * mm, "end": v(86.05, 454.42) * mm});
            skPoint(sketch, "E384.12.6.0", {"position": v(86.05, 454.42) * mm});
            skPoint(sketch, "E384.13.6.0", {"position": v(68.37, 457.42) * mm});
            skArc(sketch, "E384.3.7.0", {"start": v(103.6, 450.75) * mm, "mid": v(102.8, 442.8) * mm, "end": v(104.8, 435.06) * mm});
            skArc(sketch, "E384.4.7.0", {"start": v(104.8, 435.06) * mm, "mid": v(108.35, 433.4) * mm, "end": v(112.26, 433.19) * mm});
            skArc(sketch, "E384.8.7.0", {"start": v(112.26, 433.19) * mm, "mid": v(117.7, 439.08) * mm, "end": v(121, 446.4) * mm});
            skPoint(sketch, "E384.12.7.0", {"position": v(121, 446.4) * mm});
            skPoint(sketch, "E384.13.7.0", {"position": v(103.6, 450.75) * mm});
            skArc(sketch, "E384.3.8.0", {"start": v(138.22, 441.36) * mm, "mid": v(136.8, 433.5) * mm, "end": v(138.2, 425.63) * mm});
            skArc(sketch, "E384.4.8.0", {"start": v(138.2, 425.63) * mm, "mid": v(141.6, 423.7) * mm, "end": v(145.5, 423.19) * mm});
            skArc(sketch, "E384.8.8.0", {"start": v(145.5, 423.19) * mm, "mid": v(151.37, 428.64) * mm, "end": v(155.23, 435.67) * mm});
            skPoint(sketch, "E384.12.8.0", {"position": v(155.23, 435.67) * mm});
            skPoint(sketch, "E384.13.8.0", {"position": v(138.22, 441.36) * mm});
            skSolve(sketch);
        }
        {
            var Q0;
            {var subQ0=sQuery(id+"F18.wireOp",EDGE,"E358");Q0=makeQuery(id+"F18.imprint","IMPRINT",FACE,{"disambiguationData":[TD([[makeQuery(id+"F18.imprint","IMPRINT",EDGE,{"derivedFrom":subQ0}),1.0]])]});}
            var Q1;
            Q1=sQuery(id+"F18.wireOp",EDGE,"E358");
            var Q2;
            Q2=sQuery(id+"F18.wireOp",EDGE,"E379");
            var Q3;
            Q3=sQuery(id+"F18.wireOp",EDGE,"E362");
            var Q4;
            Q4=sQuery(id+"F18.wireOp",EDGE,"E357");
            extrude(context, id + "F19", {"entities" : qUnion([Q0]), "operationType" : NewBodyOperationType.ADD, "surfaceEntities" : qUnion([Q1, Q2, Q3, Q4]), "depth" : 5 * mm, "hasSecondDirection" : true, "secondDirectionOppositeDirection" : true, "secondDirectionDepth" : 5 * mm});
        }
        {
            var Q0;
            {var subQ6=sQuery(id+"F18.wireOp",EDGE,"E331");Q0=makeQuery(id+"F18.imprint","IMPRINT",FACE,{"disambiguationData":[TD([[makeQuery(id+"F18.imprint","IMPRINT",EDGE,{"derivedFrom":subQ6}),-1.0]])]});}
            var Q1;
            {var subQ0=sQuery(id+"F18.wireOp",EDGE,"E384.3.8.0");Q1=makeQuery(id+"F18.imprint","IMPRINT",FACE,{"disambiguationData":[TD([[makeQuery(id+"F18.imprint","IMPRINT",EDGE,{"derivedFrom":subQ0}),1.0]])]});}
            var Q2;
            {var subQ0=sQuery(id+"F18.wireOp",EDGE,"E384.3.7.0");Q2=makeQuery(id+"F18.imprint","IMPRINT",FACE,{"disambiguationData":[TD([[makeQuery(id+"F18.imprint","IMPRINT",EDGE,{"derivedFrom":subQ0}),1.0]])]});}
            var Q3;
            {var subQ0=sQuery(id+"F18.wireOp",EDGE,"E384.3.6.0");Q3=makeQuery(id+"F18.imprint","IMPRINT",FACE,{"disambiguationData":[TD([[makeQuery(id+"F18.imprint","IMPRINT",EDGE,{"derivedFrom":subQ0}),1.0]])]});}
            var Q4;
            {var subQ0=sQuery(id+"F18.wireOp",EDGE,"E384.3.5.0");Q4=makeQuery(id+"F18.imprint","IMPRINT",FACE,{"disambiguationData":[TD([[makeQuery(id+"F18.imprint","IMPRINT",EDGE,{"derivedFrom":subQ0}),1.0]])]});}
            var Q5;
            {var subQ0=sQuery(id+"F18.wireOp",EDGE,"E384.3.4.0");Q5=makeQuery(id+"F18.imprint","IMPRINT",FACE,{"disambiguationData":[TD([[makeQuery(id+"F18.imprint","IMPRINT",EDGE,{"derivedFrom":subQ0}),1.0]])]});}
            var Q6;
            {var subQ0=sQuery(id+"F18.wireOp",EDGE,"E384.3.3.0");Q6=makeQuery(id+"F18.imprint","IMPRINT",FACE,{"disambiguationData":[TD([[makeQuery(id+"F18.imprint","IMPRINT",EDGE,{"derivedFrom":subQ0}),1.0]])]});}
            var Q7;
            {var subQ0=sQuery(id+"F18.wireOp",EDGE,"E383.2.0");Q7=makeQuery(id+"F18.imprint","IMPRINT",FACE,{"disambiguationData":[TD([[makeQuery(id+"F18.imprint","IMPRINT",EDGE,{"derivedFrom":subQ0}),1.0]])]});}
            var Q8;
            {var subQ0=sQuery(id+"F18.wireOp",EDGE,"E383.1.0");Q8=makeQuery(id+"F18.imprint","IMPRINT",FACE,{"disambiguationData":[TD([[makeQuery(id+"F18.imprint","IMPRINT",EDGE,{"derivedFrom":subQ0}),1.0]])]});}
            var Q9;
            {var subQ0=sQuery(id+"F18.wireOp",EDGE,"E375");Q9=makeQuery(id+"F18.imprint","IMPRINT",FACE,{"disambiguationData":[TD([[makeQuery(id+"F18.imprint","IMPRINT",EDGE,{"derivedFrom":subQ0}),1.0]])]});}
            extrude(context, id + "F20", {"entities" : qUnion([Q0, Q1, Q2, Q3, Q4, Q5, Q6, Q7, Q8, Q9]), "operationType" : NewBodyOperationType.ADD, "depth" : 15 * mm, "hasSecondDirection" : true, "secondDirectionOppositeDirection" : true, "secondDirectionDepth" : 15 * mm});
        }
    });
